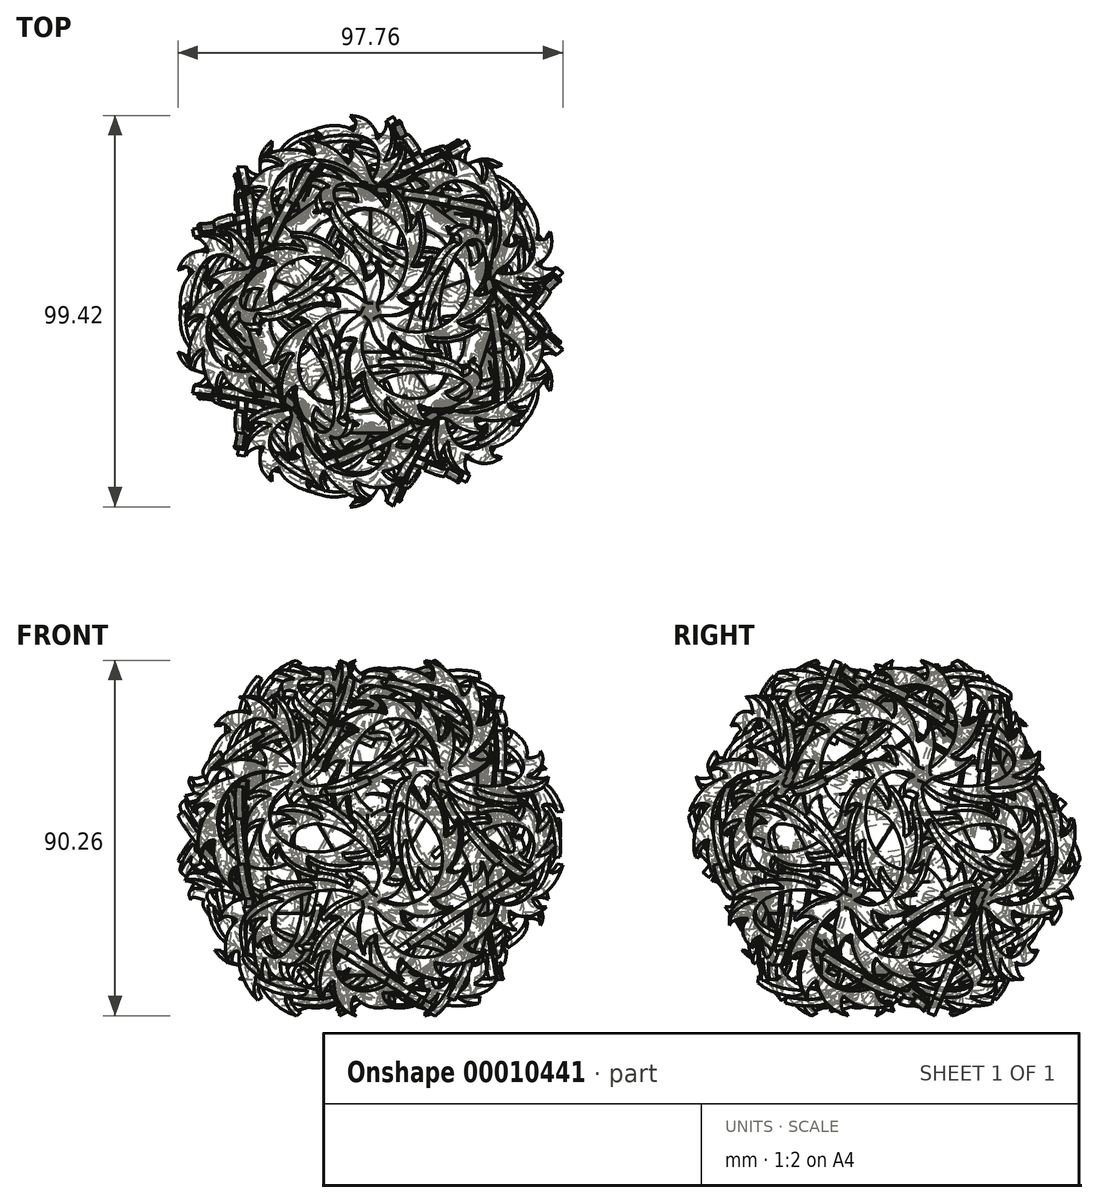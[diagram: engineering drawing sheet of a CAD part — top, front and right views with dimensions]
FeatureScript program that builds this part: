
annotation { "Feature Type Name" : "Feature", "Feature Type Description" : "" }
export const myFeature = defineFeature(function(context is Context, id is Id, definition is map)
    precondition{}
    {
        {
            var Q0;
            Q0=qCreatedBy(makeId("Top.planeOp"),FACE);
            var sketch = newSketch(context, id + "F0", { "sketchPlane" : qUnion([Q0])});
            skCircle(sketch, "E0.cCircle", {"center": v(0, 0) * mm, "radius": 10.32 * mm, "construction": true});
            skLineSegment(sketch, "E0.0", {"start": v(7.5, -10.32) * mm, "end": v(-7.5, -10.32) * mm});
            skLineSegment(sketch, "E0.1", {"start": v(-7.5, -10.32) * mm, "end": v(-12.14, 3.94) * mm});
            skLineSegment(sketch, "E0.2", {"start": v(-12.14, 3.94) * mm, "end": v(0, 12.76) * mm});
            skLineSegment(sketch, "E0.3", {"start": v(0, 12.76) * mm, "end": v(12.14, 3.94) * mm});
            skLineSegment(sketch, "E0.4", {"start": v(12.14, 3.94) * mm, "end": v(7.5, -10.32) * mm});
            skPoint(sketch, "E0.0.midPoint", {"position": v(0, -10.32) * mm});
            skLineSegment(sketch, "E1", {"start": v(0, 12.76) * mm, "end": v(0, -10.32) * mm});
            skSolve(sketch);
        }
        {
            var Q0;
            Q0=qCreatedBy(makeId("Top.planeOp"),FACE);
            var sketch = newSketch(context, id + "F1", { "sketchPlane" : qUnion([Q0])});
            skCircle(sketch, "E2.cCircle", {"center": v(22.17, -7.2) * mm, "radius": 13 * mm, "construction": true});
            skLineSegment(sketch, "E2.0", {"start": v(36.84, -4.09) * mm, "end": v(32.2, -18.35) * mm});
            skLineSegment(sketch, "E2.1", {"start": v(32.2, -18.35) * mm, "end": v(17.54, -21.47) * mm});
            skLineSegment(sketch, "E2.2", {"start": v(17.54, -21.47) * mm, "end": v(7.5, -10.32) * mm});
            skLineSegment(sketch, "E2.3", {"start": v(7.5, -10.32) * mm, "end": v(12.14, 3.94) * mm});
            skLineSegment(sketch, "E2.4", {"start": v(12.14, 3.94) * mm, "end": v(26.8, 7.06) * mm});
            skLineSegment(sketch, "E2.5", {"start": v(26.8, 7.06) * mm, "end": v(36.84, -4.09) * mm});
            skPoint(sketch, "E2.0.midPoint", {"position": v(34.53, -11.22) * mm});
            skSolve(sketch);
        }
        {
            var Q0;
            Q0=makeQuery(id+"F0.imprint","IMPRINT",FACE,{"disambiguationData":[TD([[makeQuery(id+"F0.imprint","IMPRINT",EDGE,{"derivedFrom":sQuery(id+"F0.wireOp",EDGE,"E0.0")}),-1.0]])]});
            extrude(context, id + "F2", {"entities" : qUnion([Q0]), "oppositeDirection" : true, "depth" : 1 * mm});
        }
        {
            var Q0;
            Q0=makeQuery(id+"F1.imprint","IMPRINT",FACE,{"disambiguationData":[TD([[makeQuery(id+"F1.imprint","IMPRINT",EDGE,{"derivedFrom":sQuery(id+"F1.wireOp",EDGE,"E2.0")}),-1.0]])]});
            extrude(context, id + "F3", {"entities" : qUnion([Q0]), "oppositeDirection" : true, "depth" : 1 * mm});
        }
        {
            var Q0;
            Q0=makeQuery(id+"F3.opExtrude","SWEPT_BODY",BODY,{"disambiguationData":[OSD([sQuery(id+"F1.wireOp",EDGE,"E2.0"),sQuery(id+"F1.wireOp",EDGE,"E2.1"),sQuery(id+"F1.wireOp",EDGE,"E2.2"),sQuery(id+"F1.wireOp",EDGE,"E2.3"),sQuery(id+"F1.wireOp",EDGE,"E2.4"),sQuery(id+"F1.wireOp",EDGE,"E2.5")])]});
            var Q1;
            Q1=makeQuery(id+"F2.opExtrude","CAP_EDGE",EDGE,{"disambiguationData":[OSD([sQuery(id+"F0.wireOp",EDGE,"E0.4")])],"isStart":true});
            transform(context, id + "F4", {"entities" : qUnion([Q0]), "transformType" : TransformType.ROTATION, "transformAxis" : qUnion([Q1]), "angle" : 37.38 * degree, "oppositeDirection" : true, "makeCopy" : false});
        }
        {
            var Q0;
            Q0=qCreatedBy(makeId("Right.planeOp"),FACE);
            var sketch = newSketch(context, id + "F5", { "sketchPlane" : qUnion([Q0])});
            skLineSegment(sketch, "E3", {"start": v(0, 0) * mm, "end": v(0, 7.73) * mm});
            skSolve(sketch);
        }
        {
            var Q0;
            Q0=makeQuery(id+"F3.opExtrude","SWEPT_BODY",BODY,{"disambiguationData":[OSD([sQuery(id+"F1.wireOp",EDGE,"E2.0"),sQuery(id+"F1.wireOp",EDGE,"E2.1"),sQuery(id+"F1.wireOp",EDGE,"E2.2"),sQuery(id+"F1.wireOp",EDGE,"E2.3"),sQuery(id+"F1.wireOp",EDGE,"E2.4"),sQuery(id+"F1.wireOp",EDGE,"E2.5")])]});
            var Q1;
            Q1=sQuery(id+"F5.wireOp",EDGE,"E3");
            circularPattern(context, id + "F6", {"entities" : qUnion([Q0]), "axis" : qUnion([Q1]), "angle" : 72 * degree, "instanceCount" : round(5)});
        }
        {
            var Q0;
            Q0=makeQuery(id+"F6.opPattern","COPY",FACE,{"derivedFrom":makeQuery(id+"F3.opExtrude","CAP_FACE",FACE,{"disambiguationData":[OSD([sQuery(id+"F1.wireOp",EDGE,"E2.0"),sQuery(id+"F1.wireOp",EDGE,"E2.1"),sQuery(id+"F1.wireOp",EDGE,"E2.2"),sQuery(id+"F1.wireOp",EDGE,"E2.3"),sQuery(id+"F1.wireOp",EDGE,"E2.4"),sQuery(id+"F1.wireOp",EDGE,"E2.5")])],"isStart":true}),"instanceName":"4"});
            var sketch = newSketch(context, id + "F7", { "sketchPlane" : qUnion([Q0])});
            skLineSegment(sketch, "E4", {"start": v(0, -34.18) * mm, "end": v(0, -8.2) * mm});
            skLineSegment(sketch, "E5", {"start": v(-15, -21.2) * mm, "end": v(15, -21.2) * mm});
            skCircle(sketch, "E6", {"center": v(0, -21.2) * mm, "radius": 3.24 * mm});
            skSolve(sketch);
        }
        {
            var Q0;
            Q0=qCreatedBy(makeId("Right.planeOp"),FACE);
            var sketch = newSketch(context, id + "F8", { "sketchPlane" : qUnion([Q0])});
            skArc(sketch, "E7.0", {"start": v(-1.37, 0) * mm, "mid": v(-18.04, 14.75) * mm, "end": v(-20.04, -7.42) * mm});
            skLineSegment(sketch, "E8", {"start": v(-20.04, -7.42) * mm, "end": v(-24.47, -10.8) * mm});
            skLineSegment(sketch, "E9", {"start": v(-1.37, 0) * mm, "end": v(0, 0) * mm});
            skArc(sketch, "E10", {"start": v(1.07, 1.27) * mm, "mid": v(3.46, 7.37) * mm, "end": v(2.5, 13.85) * mm});
            skArc(sketch, "E11", {"start": v(-0.8, 8.97) * mm, "mid": v(1.84, 10.74) * mm, "end": v(2.5, 13.85) * mm});
            skArc(sketch, "E12.1.0", {"start": v(-0.8, 8.97) * mm, "mid": v(-2.13, 15.94) * mm, "end": v(-6.98, 21.1) * mm});
            skArc(sketch, "E12.1.1", {"start": v(-6.75, 15.32) * mm, "mid": v(-5.72, 18.26) * mm, "end": v(-6.98, 21.1) * mm});
            skArc(sketch, "E12.2.0", {"start": v(-6.75, 15.32) * mm, "mid": v(-11.92, 20.18) * mm, "end": v(-18.89, 21.5) * mm});
            skArc(sketch, "E12.2.1", {"start": v(-15.3, 16.96) * mm, "mid": v(-16.2, 19.94) * mm, "end": v(-18.89, 21.5) * mm});
            skArc(sketch, "E12.3.0", {"start": v(-15.3, 16.96) * mm, "mid": v(-22.34, 17.85) * mm, "end": v(-28.75, 14.83) * mm});
            skArc(sketch, "E12.3.1", {"start": v(-23.18, 13.26) * mm, "mid": v(-25.66, 15.15) * mm, "end": v(-28.75, 14.83) * mm});
            skArc(sketch, "E12.4.0", {"start": v(-23.18, 13.26) * mm, "mid": v(-29.4, 9.84) * mm, "end": v(-32.81, 3.63) * mm});
            skArc(sketch, "E12.4.1", {"start": v(-27.38, 5.64) * mm, "mid": v(-30.5, 5.7) * mm, "end": v(-32.81, 3.63) * mm});
            skArc(sketch, "E12.5.0", {"start": v(-27.38, 5.64) * mm, "mid": v(-30.4, -0.78) * mm, "end": v(-29.51, -7.81) * mm});
            skArc(sketch, "E12.5.1", {"start": v(-26.3, -3) * mm, "mid": v(-28.86, -4.77) * mm, "end": v(-29.51, -7.81) * mm});
            skArc(sketch, "E12.6.0", {"start": v(-26.3, -3) * mm, "mid": v(-26.03, -7.06) * mm, "end": v(-24.49, -10.82) * mm});
            skArc(sketch, "E13", {"start": v(-24.49, -10.82) * mm, "mid": v(-20.56, -11.35) * mm, "end": v(-20.04, -7.42) * mm});
            skArc(sketch, "E14", {"start": v(-1.37, 0) * mm, "mid": v(1.27, -2.11) * mm, "end": v(1.07, 1.27) * mm});
            skSolve(sketch);
        }
        {
            var Q0;
            {var subQ2=sQuery(id+"F8.wireOp",EDGE,"E7.0");Q0=makeQuery(id+"F8.imprint","IMPRINT",FACE,{"disambiguationData":[TD([[makeQuery(id+"F8.imprint","IMPRINT",EDGE,{"derivedFrom":subQ2}),-1.0]])]});}
            extrude(context, id + "F9", {"entities" : qUnion([Q0]), "oppositeDirection" : true, "depth" : 2 * mm});
        }
        {
            var Q0;
            Q0=makeQuery(id+"F9.opExtrude","SWEPT_EDGE",EDGE,{"disambiguationData":[OSD([sQuery(id+"F8.wireOp",EDGE,"E10"),sQuery(id+"F8.wireOp",EDGE,"E14")])]});
            fillet(context, id + "F10", {"entities" : qUnion([Q0]), "radius" : 5 * mm, "tangentPropagation" : true, "allowEdgeOverflow" : false});
        }
        {
            var Q0;
            Q0=qCreatedBy(makeId("Right.planeOp"),FACE);
            var sketch = newSketch(context, id + "F11", { "sketchPlane" : qUnion([Q0])});
            skLineSegment(sketch, "E15", {"start": v(0, 0) * mm, "end": v(-20.65, -7.89) * mm});
            skLineSegment(sketch, "E16", {"start": v(0, 0) * mm, "end": v(0, 28.42) * mm});
            skSolve(sketch);
        }
        {
            var Q0;
            Q0=makeQuery(id+"F9.opExtrude","SWEPT_BODY",BODY,{"disambiguationData":[OSD([sQuery(id+"F8.wireOp",EDGE,"003f2e54-bd62-4f0b-a98e-8c36e71e2cf6"),sQuery(id+"F8.wireOp",EDGE,"8c729305-40a1-49fa-b790-4b99a3909bb6"),sQuery(id+"F8.wireOp",EDGE,"862a2a8f-3db7-4421-9c69-6ab2f53c4c24.1.0"),sQuery(id+"F8.wireOp",EDGE,"862a2a8f-3db7-4421-9c69-6ab2f53c4c24.1.1"),sQuery(id+"F8.wireOp",EDGE,"862a2a8f-3db7-4421-9c69-6ab2f53c4c24.2.0"),sQuery(id+"F8.wireOp",EDGE,"862a2a8f-3db7-4421-9c69-6ab2f53c4c24.2.1"),sQuery(id+"F8.wireOp",EDGE,"862a2a8f-3db7-4421-9c69-6ab2f53c4c24.3.0"),sQuery(id+"F8.wireOp",EDGE,"862a2a8f-3db7-4421-9c69-6ab2f53c4c24.3.1"),sQuery(id+"F8.wireOp",EDGE,"862a2a8f-3db7-4421-9c69-6ab2f53c4c24.4.0"),sQuery(id+"F8.wireOp",EDGE,"862a2a8f-3db7-4421-9c69-6ab2f53c4c24.4.1"),sQuery(id+"F8.wireOp",EDGE,"862a2a8f-3db7-4421-9c69-6ab2f53c4c24.5.0"),sQuery(id+"F8.wireOp",EDGE,"E7.0"),sQuery(id+"F8.wireOp",EDGE,"E8"),sQuery(id+"F8.wireOp",EDGE,"E9")])]});
            var Q1;
            Q1=sQuery(id+"F11.wireOp",EDGE,"E15");
            transform(context, id + "F12", {"entities" : qUnion([Q0]), "transformType" : TransformType.ROTATION, "transformAxis" : qUnion([Q1]), "angle" : 65 * degree, "makeCopy" : false});
        }
        {
            var Q0;
            Q0=makeQuery(id+"F9.opExtrude","SWEPT_BODY",BODY,{"disambiguationData":[OSD([sQuery(id+"F8.wireOp",EDGE,"003f2e54-bd62-4f0b-a98e-8c36e71e2cf6"),sQuery(id+"F8.wireOp",EDGE,"8c729305-40a1-49fa-b790-4b99a3909bb6"),sQuery(id+"F8.wireOp",EDGE,"862a2a8f-3db7-4421-9c69-6ab2f53c4c24.1.0"),sQuery(id+"F8.wireOp",EDGE,"862a2a8f-3db7-4421-9c69-6ab2f53c4c24.1.1"),sQuery(id+"F8.wireOp",EDGE,"862a2a8f-3db7-4421-9c69-6ab2f53c4c24.2.0"),sQuery(id+"F8.wireOp",EDGE,"862a2a8f-3db7-4421-9c69-6ab2f53c4c24.2.1"),sQuery(id+"F8.wireOp",EDGE,"862a2a8f-3db7-4421-9c69-6ab2f53c4c24.3.0"),sQuery(id+"F8.wireOp",EDGE,"862a2a8f-3db7-4421-9c69-6ab2f53c4c24.3.1"),sQuery(id+"F8.wireOp",EDGE,"862a2a8f-3db7-4421-9c69-6ab2f53c4c24.4.0"),sQuery(id+"F8.wireOp",EDGE,"862a2a8f-3db7-4421-9c69-6ab2f53c4c24.4.1"),sQuery(id+"F8.wireOp",EDGE,"862a2a8f-3db7-4421-9c69-6ab2f53c4c24.5.0"),sQuery(id+"F8.wireOp",EDGE,"E7.0"),sQuery(id+"F8.wireOp",EDGE,"E8"),sQuery(id+"F8.wireOp",EDGE,"E9")])]});
            var Q1;
            Q1=sQuery(id+"F11.wireOp",EDGE,"E16");
            circularPattern(context, id + "F13", {"entities" : qUnion([Q0]), "axis" : qUnion([Q1]), "angle" : 72 * degree, "instanceCount" : round(5)});
        }
        {
            var Q0;
            Q0=qCreatedBy(makeId("Right.planeOp"),FACE);
            var sketch = newSketch(context, id + "F14", { "sketchPlane" : qUnion([Q0])});
            skLineSegment(sketch, "E17.0", {"start": v(-30.97, -15.77) * mm, "end": v(-10.32, 0) * mm});
            skLineSegment(sketch, "E18", {"start": v(-20.65, -7.89) * mm, "end": v(-30.05, 4.42) * mm});
            skSolve(sketch);
        }
        {
            var Q0;
            Q0=makeQuery(id+"F9.opExtrude","SWEPT_BODY",BODY,{"disambiguationData":[OSD([sQuery(id+"F8.wireOp",EDGE,"003f2e54-bd62-4f0b-a98e-8c36e71e2cf6"),sQuery(id+"F8.wireOp",EDGE,"8c729305-40a1-49fa-b790-4b99a3909bb6"),sQuery(id+"F8.wireOp",EDGE,"862a2a8f-3db7-4421-9c69-6ab2f53c4c24.1.0"),sQuery(id+"F8.wireOp",EDGE,"862a2a8f-3db7-4421-9c69-6ab2f53c4c24.1.1"),sQuery(id+"F8.wireOp",EDGE,"862a2a8f-3db7-4421-9c69-6ab2f53c4c24.2.0"),sQuery(id+"F8.wireOp",EDGE,"862a2a8f-3db7-4421-9c69-6ab2f53c4c24.2.1"),sQuery(id+"F8.wireOp",EDGE,"862a2a8f-3db7-4421-9c69-6ab2f53c4c24.3.0"),sQuery(id+"F8.wireOp",EDGE,"862a2a8f-3db7-4421-9c69-6ab2f53c4c24.3.1"),sQuery(id+"F8.wireOp",EDGE,"862a2a8f-3db7-4421-9c69-6ab2f53c4c24.4.0"),sQuery(id+"F8.wireOp",EDGE,"862a2a8f-3db7-4421-9c69-6ab2f53c4c24.4.1"),sQuery(id+"F8.wireOp",EDGE,"862a2a8f-3db7-4421-9c69-6ab2f53c4c24.5.0"),sQuery(id+"F8.wireOp",EDGE,"E7.0"),sQuery(id+"F8.wireOp",EDGE,"E8"),sQuery(id+"F8.wireOp",EDGE,"E9")])]});
            var Q1;
            Q1=sQuery(id+"F14.wireOp",EDGE,"E18");
            circularPattern(context, id + "F15", {"entities" : qUnion([Q0]), "axis" : qUnion([Q1]), "angle" : 120 * degree, "instanceCount" : round(3)});
        }
        {
            var Q0;
            Q0=makeQuery(id+"F15.opPattern","COPY",BODY,{"derivedFrom":makeQuery(id+"F9.opExtrude","SWEPT_BODY",BODY,{"disambiguationData":[OSD([sQuery(id+"F8.wireOp",EDGE,"E7.0"),sQuery(id+"F8.wireOp",EDGE,"E10"),sQuery(id+"F8.wireOp",EDGE,"E11"),sQuery(id+"F8.wireOp",EDGE,"E12.1.0"),sQuery(id+"F8.wireOp",EDGE,"E12.1.1"),sQuery(id+"F8.wireOp",EDGE,"E12.2.0"),sQuery(id+"F8.wireOp",EDGE,"E12.2.1"),sQuery(id+"F8.wireOp",EDGE,"E12.3.0"),sQuery(id+"F8.wireOp",EDGE,"E12.3.1"),sQuery(id+"F8.wireOp",EDGE,"E12.4.0"),sQuery(id+"F8.wireOp",EDGE,"E12.4.1"),sQuery(id+"F8.wireOp",EDGE,"E12.5.0"),sQuery(id+"F8.wireOp",EDGE,"E12.5.1"),sQuery(id+"F8.wireOp",EDGE,"E12.6.0"),sQuery(id+"F8.wireOp",EDGE,"E13"),sQuery(id+"F8.wireOp",EDGE,"E14")])]}),"instanceName":"2"});
            var Q1;
            Q1=makeQuery(id+"F15.opPattern","COPY",BODY,{"derivedFrom":makeQuery(id+"F9.opExtrude","SWEPT_BODY",BODY,{"disambiguationData":[OSD([sQuery(id+"F8.wireOp",EDGE,"E7.0"),sQuery(id+"F8.wireOp",EDGE,"E10"),sQuery(id+"F8.wireOp",EDGE,"E11"),sQuery(id+"F8.wireOp",EDGE,"E12.1.0"),sQuery(id+"F8.wireOp",EDGE,"E12.1.1"),sQuery(id+"F8.wireOp",EDGE,"E12.2.0"),sQuery(id+"F8.wireOp",EDGE,"E12.2.1"),sQuery(id+"F8.wireOp",EDGE,"E12.3.0"),sQuery(id+"F8.wireOp",EDGE,"E12.3.1"),sQuery(id+"F8.wireOp",EDGE,"E12.4.0"),sQuery(id+"F8.wireOp",EDGE,"E12.4.1"),sQuery(id+"F8.wireOp",EDGE,"E12.5.0"),sQuery(id+"F8.wireOp",EDGE,"E12.5.1"),sQuery(id+"F8.wireOp",EDGE,"E12.6.0"),sQuery(id+"F8.wireOp",EDGE,"E13"),sQuery(id+"F8.wireOp",EDGE,"E14")])]}),"instanceName":"1"});
            var Q2;
            Q2=sQuery(id+"F11.wireOp",EDGE,"E16");
            circularPattern(context, id + "F16", {"entities" : qUnion([Q0, Q1]), "axis" : qUnion([Q2]), "angle" : 72 * degree, "instanceCount" : round(5)});
        }
        {
            var Q0;
            Q0=makeQuery(id+"F3.opExtrude","SWEPT_BODY",BODY,{"disambiguationData":[OSD([sQuery(id+"F1.wireOp",EDGE,"E2.0"),sQuery(id+"F1.wireOp",EDGE,"E2.1"),sQuery(id+"F1.wireOp",EDGE,"E2.2"),sQuery(id+"F1.wireOp",EDGE,"E2.3"),sQuery(id+"F1.wireOp",EDGE,"E2.4"),sQuery(id+"F1.wireOp",EDGE,"E2.5")])]});
            var Q1;
            Q1=makeQuery(id+"F16.opPattern","COPY",BODY,{"derivedFrom":makeQuery(id+"F15.opPattern","COPY",BODY,{"derivedFrom":makeQuery(id+"F9.opExtrude","SWEPT_BODY",BODY,{"disambiguationData":[OSD([sQuery(id+"F8.wireOp",EDGE,"E7.0"),sQuery(id+"F8.wireOp",EDGE,"E10"),sQuery(id+"F8.wireOp",EDGE,"E11"),sQuery(id+"F8.wireOp",EDGE,"E12.1.0"),sQuery(id+"F8.wireOp",EDGE,"E12.1.1"),sQuery(id+"F8.wireOp",EDGE,"E12.2.0"),sQuery(id+"F8.wireOp",EDGE,"E12.2.1"),sQuery(id+"F8.wireOp",EDGE,"E12.3.0"),sQuery(id+"F8.wireOp",EDGE,"E12.3.1"),sQuery(id+"F8.wireOp",EDGE,"E12.4.0"),sQuery(id+"F8.wireOp",EDGE,"E12.4.1"),sQuery(id+"F8.wireOp",EDGE,"E12.5.0"),sQuery(id+"F8.wireOp",EDGE,"E12.5.1"),sQuery(id+"F8.wireOp",EDGE,"E12.6.0"),sQuery(id+"F8.wireOp",EDGE,"E13"),sQuery(id+"F8.wireOp",EDGE,"E14")])]}),"instanceName":"1"}),"instanceName":"1"});
            var Q2;
            Q2=makeQuery(id+"F13.opPattern","COPY",BODY,{"derivedFrom":makeQuery(id+"F9.opExtrude","SWEPT_BODY",BODY,{"disambiguationData":[OSD([sQuery(id+"F8.wireOp",EDGE,"E7.0"),sQuery(id+"F8.wireOp",EDGE,"E10"),sQuery(id+"F8.wireOp",EDGE,"E11"),sQuery(id+"F8.wireOp",EDGE,"E12.1.0"),sQuery(id+"F8.wireOp",EDGE,"E12.1.1"),sQuery(id+"F8.wireOp",EDGE,"E12.2.0"),sQuery(id+"F8.wireOp",EDGE,"E12.2.1"),sQuery(id+"F8.wireOp",EDGE,"E12.3.0"),sQuery(id+"F8.wireOp",EDGE,"E12.3.1"),sQuery(id+"F8.wireOp",EDGE,"E12.4.0"),sQuery(id+"F8.wireOp",EDGE,"E12.4.1"),sQuery(id+"F8.wireOp",EDGE,"E12.5.0"),sQuery(id+"F8.wireOp",EDGE,"E12.5.1"),sQuery(id+"F8.wireOp",EDGE,"E12.6.0"),sQuery(id+"F8.wireOp",EDGE,"E13"),sQuery(id+"F8.wireOp",EDGE,"E14")])]}),"instanceName":"1"});
            var Q3;
            Q3=makeQuery(id+"F16.opPattern","COPY",BODY,{"derivedFrom":makeQuery(id+"F15.opPattern","COPY",BODY,{"derivedFrom":makeQuery(id+"F9.opExtrude","SWEPT_BODY",BODY,{"disambiguationData":[OSD([sQuery(id+"F8.wireOp",EDGE,"E7.0"),sQuery(id+"F8.wireOp",EDGE,"E10"),sQuery(id+"F8.wireOp",EDGE,"E11"),sQuery(id+"F8.wireOp",EDGE,"E12.1.0"),sQuery(id+"F8.wireOp",EDGE,"E12.1.1"),sQuery(id+"F8.wireOp",EDGE,"E12.2.0"),sQuery(id+"F8.wireOp",EDGE,"E12.2.1"),sQuery(id+"F8.wireOp",EDGE,"E12.3.0"),sQuery(id+"F8.wireOp",EDGE,"E12.3.1"),sQuery(id+"F8.wireOp",EDGE,"E12.4.0"),sQuery(id+"F8.wireOp",EDGE,"E12.4.1"),sQuery(id+"F8.wireOp",EDGE,"E12.5.0"),sQuery(id+"F8.wireOp",EDGE,"E12.5.1"),sQuery(id+"F8.wireOp",EDGE,"E12.6.0"),sQuery(id+"F8.wireOp",EDGE,"E13"),sQuery(id+"F8.wireOp",EDGE,"E14")])]}),"instanceName":"2"}),"instanceName":"1"});
            var Q4;
            Q4=sQuery(id+"F14.wireOp",EDGE,"E18");
            circularPattern(context, id + "F17", {"entities" : qUnion([Q0, Q1, Q2, Q3]), "axis" : qUnion([Q4]), "angle" : 120 * degree, "instanceCount" : 2, "oppositeDirection" : true});
        }
        {
            var Q0;
            Q0=makeQuery(id+"F2.opExtrude","SWEPT_BODY",BODY,{"disambiguationData":[OSD([sQuery(id+"F0.wireOp",EDGE,"E0.0"),sQuery(id+"F0.wireOp",EDGE,"E0.1"),sQuery(id+"F0.wireOp",EDGE,"E0.2"),sQuery(id+"F0.wireOp",EDGE,"E0.3"),sQuery(id+"F0.wireOp",EDGE,"E0.4")])]});
            var Q1;
            Q1=makeQuery(id+"F13.opPattern","COPY",BODY,{"derivedFrom":makeQuery(id+"F9.opExtrude","SWEPT_BODY",BODY,{"disambiguationData":[OSD([sQuery(id+"F8.wireOp",EDGE,"E7.0"),sQuery(id+"F8.wireOp",EDGE,"E10"),sQuery(id+"F8.wireOp",EDGE,"E11"),sQuery(id+"F8.wireOp",EDGE,"E12.1.0"),sQuery(id+"F8.wireOp",EDGE,"E12.1.1"),sQuery(id+"F8.wireOp",EDGE,"E12.2.0"),sQuery(id+"F8.wireOp",EDGE,"E12.2.1"),sQuery(id+"F8.wireOp",EDGE,"E12.3.0"),sQuery(id+"F8.wireOp",EDGE,"E12.3.1"),sQuery(id+"F8.wireOp",EDGE,"E12.4.0"),sQuery(id+"F8.wireOp",EDGE,"E12.4.1"),sQuery(id+"F8.wireOp",EDGE,"E12.5.0"),sQuery(id+"F8.wireOp",EDGE,"E12.5.1"),sQuery(id+"F8.wireOp",EDGE,"E12.6.0"),sQuery(id+"F8.wireOp",EDGE,"E13"),sQuery(id+"F8.wireOp",EDGE,"E14")])]}),"instanceName":"2"});
            var Q2;
            Q2=makeQuery(id+"F13.opPattern","COPY",BODY,{"derivedFrom":makeQuery(id+"F9.opExtrude","SWEPT_BODY",BODY,{"disambiguationData":[OSD([sQuery(id+"F8.wireOp",EDGE,"E7.0"),sQuery(id+"F8.wireOp",EDGE,"E10"),sQuery(id+"F8.wireOp",EDGE,"E11"),sQuery(id+"F8.wireOp",EDGE,"E12.1.0"),sQuery(id+"F8.wireOp",EDGE,"E12.1.1"),sQuery(id+"F8.wireOp",EDGE,"E12.2.0"),sQuery(id+"F8.wireOp",EDGE,"E12.2.1"),sQuery(id+"F8.wireOp",EDGE,"E12.3.0"),sQuery(id+"F8.wireOp",EDGE,"E12.3.1"),sQuery(id+"F8.wireOp",EDGE,"E12.4.0"),sQuery(id+"F8.wireOp",EDGE,"E12.4.1"),sQuery(id+"F8.wireOp",EDGE,"E12.5.0"),sQuery(id+"F8.wireOp",EDGE,"E12.5.1"),sQuery(id+"F8.wireOp",EDGE,"E12.6.0"),sQuery(id+"F8.wireOp",EDGE,"E13"),sQuery(id+"F8.wireOp",EDGE,"E14")])]}),"instanceName":"3"});
            var Q3;
            Q3=sQuery(id+"F14.wireOp",EDGE,"E18");
            circularPattern(context, id + "F18", {"entities" : qUnion([Q0, Q1, Q2]), "axis" : qUnion([Q3]), "angle" : 120 * degree, "instanceCount" : round(3)});
        }
        {
            var Q0;
            Q0=makeQuery(id+"F18.opPattern","COPY",FACE,{"derivedFrom":makeQuery(id+"F2.opExtrude","CAP_FACE",FACE,{"disambiguationData":[OSD([sQuery(id+"F0.wireOp",EDGE,"E0.0"),sQuery(id+"F0.wireOp",EDGE,"E0.1"),sQuery(id+"F0.wireOp",EDGE,"E0.2"),sQuery(id+"F0.wireOp",EDGE,"E0.3"),sQuery(id+"F0.wireOp",EDGE,"E0.4")])],"isStart":true}),"instanceName":"1"});
            var sketch = newSketch(context, id + "F19", { "sketchPlane" : qUnion([Q0])});
            skLineSegment(sketch, "E19", {"start": v(-1.3, -23.63) * mm, "end": v(-19.97, -37.2) * mm});
            skLineSegment(sketch, "E20", {"start": v(-19.97, -22.2) * mm, "end": v(-1.3, -35.77) * mm});
            skSolve(sketch);
        }
        {
            var Q0;
            Q0=sQuery(id+"F19.wireOp",VERTEX,"E19.end");
            var Q1;
            Q1=sQuery(id+"F19.wireOp",VERTEX,"E19.start");
            var Q2;
            Q2=sQuery(id+"F14.wireOp",VERTEX,"E18.end");
            cPlane(context, id + "F20", {"entities" : qUnion([Q0, Q1, Q2]), "cplaneType" : CPlaneType.THREE_POINT, "offset" : 150 * mm, "width" : 150 * mm, "height" : 150 * mm});
        }
        {
            var Q0;
            Q0=qCreatedBy(id+"F20.planeOp",FACE);
            var sketch = newSketch(context, id + "F21", { "sketchPlane" : qUnion([Q0])});
            skLineSegment(sketch, "E21.0", {"start": v(23.59, 6.27) * mm, "end": v(41.93, -7.75) * mm});
            skLineSegment(sketch, "E21.1", {"start": v(34.92, -2.4) * mm, "end": v(29.26, 1.94) * mm});
            skLineSegment(sketch, "E22", {"start": v(31.8, 0) * mm, "end": v(33.22, 1.87) * mm});
            skLineSegment(sketch, "E23", {"start": v(33.22, 1.87) * mm, "end": v(37.58, 7.58) * mm});
            skSolve(sketch);
        }
        {
            var Q0;
            Q0=makeQuery(id+"F17.opPattern","COPY",BODY,{"derivedFrom":makeQuery(id+"F3.opExtrude","SWEPT_BODY",BODY,{"disambiguationData":[OSD([sQuery(id+"F1.wireOp",EDGE,"E2.0"),sQuery(id+"F1.wireOp",EDGE,"E2.1"),sQuery(id+"F1.wireOp",EDGE,"E2.2"),sQuery(id+"F1.wireOp",EDGE,"E2.3"),sQuery(id+"F1.wireOp",EDGE,"E2.4"),sQuery(id+"F1.wireOp",EDGE,"E2.5")])]}),"instanceName":"1"});
            var Q1;
            Q1=makeQuery(id+"F17.opPattern","COPY",BODY,{"derivedFrom":makeQuery(id+"F13.opPattern","COPY",BODY,{"derivedFrom":makeQuery(id+"F9.opExtrude","SWEPT_BODY",BODY,{"disambiguationData":[OSD([sQuery(id+"F8.wireOp",EDGE,"E7.0"),sQuery(id+"F8.wireOp",EDGE,"E10"),sQuery(id+"F8.wireOp",EDGE,"E11"),sQuery(id+"F8.wireOp",EDGE,"E12.1.0"),sQuery(id+"F8.wireOp",EDGE,"E12.1.1"),sQuery(id+"F8.wireOp",EDGE,"E12.2.0"),sQuery(id+"F8.wireOp",EDGE,"E12.2.1"),sQuery(id+"F8.wireOp",EDGE,"E12.3.0"),sQuery(id+"F8.wireOp",EDGE,"E12.3.1"),sQuery(id+"F8.wireOp",EDGE,"E12.4.0"),sQuery(id+"F8.wireOp",EDGE,"E12.4.1"),sQuery(id+"F8.wireOp",EDGE,"E12.5.0"),sQuery(id+"F8.wireOp",EDGE,"E12.5.1"),sQuery(id+"F8.wireOp",EDGE,"E12.6.0"),sQuery(id+"F8.wireOp",EDGE,"E13"),sQuery(id+"F8.wireOp",EDGE,"E14")])]}),"instanceName":"1"}),"instanceName":"1"});
            var Q2;
            Q2=makeQuery(id+"F17.opPattern","COPY",BODY,{"derivedFrom":makeQuery(id+"F16.opPattern","COPY",BODY,{"derivedFrom":makeQuery(id+"F15.opPattern","COPY",BODY,{"derivedFrom":makeQuery(id+"F9.opExtrude","SWEPT_BODY",BODY,{"disambiguationData":[OSD([sQuery(id+"F8.wireOp",EDGE,"E7.0"),sQuery(id+"F8.wireOp",EDGE,"E10"),sQuery(id+"F8.wireOp",EDGE,"E11"),sQuery(id+"F8.wireOp",EDGE,"E12.1.0"),sQuery(id+"F8.wireOp",EDGE,"E12.1.1"),sQuery(id+"F8.wireOp",EDGE,"E12.2.0"),sQuery(id+"F8.wireOp",EDGE,"E12.2.1"),sQuery(id+"F8.wireOp",EDGE,"E12.3.0"),sQuery(id+"F8.wireOp",EDGE,"E12.3.1"),sQuery(id+"F8.wireOp",EDGE,"E12.4.0"),sQuery(id+"F8.wireOp",EDGE,"E12.4.1"),sQuery(id+"F8.wireOp",EDGE,"E12.5.0"),sQuery(id+"F8.wireOp",EDGE,"E12.5.1"),sQuery(id+"F8.wireOp",EDGE,"E12.6.0"),sQuery(id+"F8.wireOp",EDGE,"E13"),sQuery(id+"F8.wireOp",EDGE,"E14")])]}),"instanceName":"2"}),"instanceName":"1"}),"instanceName":"1"});
            var Q3;
            Q3=makeQuery(id+"F17.opPattern","COPY",BODY,{"derivedFrom":makeQuery(id+"F16.opPattern","COPY",BODY,{"derivedFrom":makeQuery(id+"F15.opPattern","COPY",BODY,{"derivedFrom":makeQuery(id+"F9.opExtrude","SWEPT_BODY",BODY,{"disambiguationData":[OSD([sQuery(id+"F8.wireOp",EDGE,"E7.0"),sQuery(id+"F8.wireOp",EDGE,"E10"),sQuery(id+"F8.wireOp",EDGE,"E11"),sQuery(id+"F8.wireOp",EDGE,"E12.1.0"),sQuery(id+"F8.wireOp",EDGE,"E12.1.1"),sQuery(id+"F8.wireOp",EDGE,"E12.2.0"),sQuery(id+"F8.wireOp",EDGE,"E12.2.1"),sQuery(id+"F8.wireOp",EDGE,"E12.3.0"),sQuery(id+"F8.wireOp",EDGE,"E12.3.1"),sQuery(id+"F8.wireOp",EDGE,"E12.4.0"),sQuery(id+"F8.wireOp",EDGE,"E12.4.1"),sQuery(id+"F8.wireOp",EDGE,"E12.5.0"),sQuery(id+"F8.wireOp",EDGE,"E12.5.1"),sQuery(id+"F8.wireOp",EDGE,"E12.6.0"),sQuery(id+"F8.wireOp",EDGE,"E13"),sQuery(id+"F8.wireOp",EDGE,"E14")])]}),"instanceName":"1"}),"instanceName":"1"}),"instanceName":"1"});
            var Q4;
            Q4=sQuery(id+"F21.wireOp",EDGE,"E22");
            circularPattern(context, id + "F22", {"entities" : qUnion([Q0, Q1, Q2, Q3]), "axis" : qUnion([Q4]), "angle" : 72 * degree, "instanceCount" : round(3), "oppositeDirection" : true});
        }
        {
            var Q0;
            Q0=makeQuery(id+"F18.opPattern","COPY",FACE,{"derivedFrom":makeQuery(id+"F2.opExtrude","CAP_FACE",FACE,{"disambiguationData":[OSD([sQuery(id+"F0.wireOp",EDGE,"E0.0"),sQuery(id+"F0.wireOp",EDGE,"E0.1"),sQuery(id+"F0.wireOp",EDGE,"E0.2"),sQuery(id+"F0.wireOp",EDGE,"E0.3"),sQuery(id+"F0.wireOp",EDGE,"E0.4")])],"isStart":true}),"instanceName":"2"});
            var sketch = newSketch(context, id + "F23", { "sketchPlane" : qUnion([Q0])});
            skLineSegment(sketch, "E24", {"start": v(1.3, -23.63) * mm, "end": v(19.97, -37.2) * mm});
            skLineSegment(sketch, "E25", {"start": v(5.7, -41.83) * mm, "end": v(12.84, -19.88) * mm});
            skSolve(sketch);
        }
        {
            var Q0;
            Q0=sQuery(id+"F23.wireOp",VERTEX,"E24.end");
            var Q1;
            Q1=sQuery(id+"F23.wireOp",VERTEX,"E24.start");
            var Q2;
            Q2=sQuery(id+"F14.wireOp",VERTEX,"E18.end");
            cPlane(context, id + "F24", {"entities" : qUnion([Q0, Q1, Q2]), "cplaneType" : CPlaneType.THREE_POINT, "offset" : 150 * mm, "width" : 150 * mm, "height" : 150 * mm});
        }
        {
            var Q0;
            Q0=qCreatedBy(id+"F24.planeOp",FACE);
            var sketch = newSketch(context, id + "F25", { "sketchPlane" : qUnion([Q0])});
            skLineSegment(sketch, "E26.0", {"start": v(23.59, 6.27) * mm, "end": v(41.93, -7.75) * mm});
            skLineSegment(sketch, "E26.1", {"start": v(34.92, -2.4) * mm, "end": v(29.26, 1.94) * mm});
            skLineSegment(sketch, "E27", {"start": v(31.8, 0) * mm, "end": v(36.23, 5.8) * mm});
            skSolve(sketch);
        }
        {
            var Q0;
            Q0=makeQuery(id+"F3.opExtrude","SWEPT_BODY",BODY,{"disambiguationData":[OSD([sQuery(id+"F1.wireOp",EDGE,"E2.0"),sQuery(id+"F1.wireOp",EDGE,"E2.1"),sQuery(id+"F1.wireOp",EDGE,"E2.2"),sQuery(id+"F1.wireOp",EDGE,"E2.3"),sQuery(id+"F1.wireOp",EDGE,"E2.4"),sQuery(id+"F1.wireOp",EDGE,"E2.5")])]});
            var Q1;
            Q1=makeQuery(id+"F16.opPattern","COPY",BODY,{"derivedFrom":makeQuery(id+"F15.opPattern","COPY",BODY,{"derivedFrom":makeQuery(id+"F9.opExtrude","SWEPT_BODY",BODY,{"disambiguationData":[OSD([sQuery(id+"F8.wireOp",EDGE,"E7.0"),sQuery(id+"F8.wireOp",EDGE,"E10"),sQuery(id+"F8.wireOp",EDGE,"E11"),sQuery(id+"F8.wireOp",EDGE,"E12.1.0"),sQuery(id+"F8.wireOp",EDGE,"E12.1.1"),sQuery(id+"F8.wireOp",EDGE,"E12.2.0"),sQuery(id+"F8.wireOp",EDGE,"E12.2.1"),sQuery(id+"F8.wireOp",EDGE,"E12.3.0"),sQuery(id+"F8.wireOp",EDGE,"E12.3.1"),sQuery(id+"F8.wireOp",EDGE,"E12.4.0"),sQuery(id+"F8.wireOp",EDGE,"E12.4.1"),sQuery(id+"F8.wireOp",EDGE,"E12.5.0"),sQuery(id+"F8.wireOp",EDGE,"E12.5.1"),sQuery(id+"F8.wireOp",EDGE,"E12.6.0"),sQuery(id+"F8.wireOp",EDGE,"E13"),sQuery(id+"F8.wireOp",EDGE,"E14")])]}),"instanceName":"2"}),"instanceName":"1"});
            var Q2;
            Q2=makeQuery(id+"F13.opPattern","COPY",BODY,{"derivedFrom":makeQuery(id+"F9.opExtrude","SWEPT_BODY",BODY,{"disambiguationData":[OSD([sQuery(id+"F8.wireOp",EDGE,"E7.0"),sQuery(id+"F8.wireOp",EDGE,"E10"),sQuery(id+"F8.wireOp",EDGE,"E11"),sQuery(id+"F8.wireOp",EDGE,"E12.1.0"),sQuery(id+"F8.wireOp",EDGE,"E12.1.1"),sQuery(id+"F8.wireOp",EDGE,"E12.2.0"),sQuery(id+"F8.wireOp",EDGE,"E12.2.1"),sQuery(id+"F8.wireOp",EDGE,"E12.3.0"),sQuery(id+"F8.wireOp",EDGE,"E12.3.1"),sQuery(id+"F8.wireOp",EDGE,"E12.4.0"),sQuery(id+"F8.wireOp",EDGE,"E12.4.1"),sQuery(id+"F8.wireOp",EDGE,"E12.5.0"),sQuery(id+"F8.wireOp",EDGE,"E12.5.1"),sQuery(id+"F8.wireOp",EDGE,"E12.6.0"),sQuery(id+"F8.wireOp",EDGE,"E13"),sQuery(id+"F8.wireOp",EDGE,"E14")])]}),"instanceName":"1"});
            var Q3;
            Q3=makeQuery(id+"F16.opPattern","COPY",BODY,{"derivedFrom":makeQuery(id+"F15.opPattern","COPY",BODY,{"derivedFrom":makeQuery(id+"F9.opExtrude","SWEPT_BODY",BODY,{"disambiguationData":[OSD([sQuery(id+"F8.wireOp",EDGE,"E7.0"),sQuery(id+"F8.wireOp",EDGE,"E10"),sQuery(id+"F8.wireOp",EDGE,"E11"),sQuery(id+"F8.wireOp",EDGE,"E12.1.0"),sQuery(id+"F8.wireOp",EDGE,"E12.1.1"),sQuery(id+"F8.wireOp",EDGE,"E12.2.0"),sQuery(id+"F8.wireOp",EDGE,"E12.2.1"),sQuery(id+"F8.wireOp",EDGE,"E12.3.0"),sQuery(id+"F8.wireOp",EDGE,"E12.3.1"),sQuery(id+"F8.wireOp",EDGE,"E12.4.0"),sQuery(id+"F8.wireOp",EDGE,"E12.4.1"),sQuery(id+"F8.wireOp",EDGE,"E12.5.0"),sQuery(id+"F8.wireOp",EDGE,"E12.5.1"),sQuery(id+"F8.wireOp",EDGE,"E12.6.0"),sQuery(id+"F8.wireOp",EDGE,"E13"),sQuery(id+"F8.wireOp",EDGE,"E14")])]}),"instanceName":"1"}),"instanceName":"1"});
            var Q4;
            Q4=sQuery(id+"F25.wireOp",EDGE,"E27");
            circularPattern(context, id + "F26", {"entities" : qUnion([Q0, Q1, Q2, Q3]), "axis" : qUnion([Q4]), "angle" : 72 * degree, "instanceCount" : round(3), "oppositeDirection" : true});
        }
        {
            var Q0;
            Q0=makeQuery(id+"F17.opPattern","COPY",FACE,{"derivedFrom":makeQuery(id+"F3.opExtrude","CAP_FACE",FACE,{"disambiguationData":[OSD([sQuery(id+"F1.wireOp",EDGE,"E2.0"),sQuery(id+"F1.wireOp",EDGE,"E2.1"),sQuery(id+"F1.wireOp",EDGE,"E2.2"),sQuery(id+"F1.wireOp",EDGE,"E2.3"),sQuery(id+"F1.wireOp",EDGE,"E2.4"),sQuery(id+"F1.wireOp",EDGE,"E2.5")])],"isStart":true}),"instanceName":"1"});
            var sketch = newSketch(context, id + "F27", { "sketchPlane" : qUnion([Q0])});
            skLineSegment(sketch, "E28", {"start": v(0, -47.28) * mm, "end": v(0, -21.3) * mm});
            skSolve(sketch);
        }
        {
            var Q0;
            Q0=qCreatedBy(makeId("Right.planeOp"),FACE);
            var sketch = newSketch(context, id + "F28", { "sketchPlane" : qUnion([Q0])});
            skLineSegment(sketch, "E29.0", {"start": v(-35.84, -41.3) * mm, "end": v(-30.97, -15.77) * mm});
            skLineSegment(sketch, "E30", {"start": v(-33.4, -28.53) * mm, "end": v(-47.6, -25.82) * mm});
            skSolve(sketch);
        }
        {
            var Q0;
            Q0=makeQuery(id+"F18.opPattern","COPY",BODY,{"derivedFrom":makeQuery(id+"F2.opExtrude","SWEPT_BODY",BODY,{"disambiguationData":[OSD([sQuery(id+"F0.wireOp",EDGE,"E0.0"),sQuery(id+"F0.wireOp",EDGE,"E0.1"),sQuery(id+"F0.wireOp",EDGE,"E0.2"),sQuery(id+"F0.wireOp",EDGE,"E0.3"),sQuery(id+"F0.wireOp",EDGE,"E0.4")])]}),"instanceName":"2"});
            var Q1;
            Q1=sQuery(id+"F28.wireOp",EDGE,"E30");
            circularPattern(context, id + "F29", {"entities" : qUnion([Q0]), "axis" : qUnion([Q1]), "angle" : 120 * degree, "instanceCount" : 2, "oppositeDirection" : true});
        }
        {
            var Q0;
            Q0=makeQuery(id+"F29.opPattern","COPY",FACE,{"derivedFrom":makeQuery(id+"F18.opPattern","COPY",FACE,{"derivedFrom":makeQuery(id+"F2.opExtrude","CAP_FACE",FACE,{"disambiguationData":[OSD([sQuery(id+"F0.wireOp",EDGE,"E0.0"),sQuery(id+"F0.wireOp",EDGE,"E0.1"),sQuery(id+"F0.wireOp",EDGE,"E0.2"),sQuery(id+"F0.wireOp",EDGE,"E0.3"),sQuery(id+"F0.wireOp",EDGE,"E0.4")])],"isStart":true}),"instanceName":"2"}),"instanceName":"1"});
            var sketch = newSketch(context, id + "F30", { "sketchPlane" : qUnion([Q0])});
            skLineSegment(sketch, "E31", {"start": v(0, -43.99) * mm, "end": v(0, -31.23) * mm});
            skLineSegment(sketch, "E32", {"start": v(-12.14, -35.17) * mm, "end": v(9.82, -28.04) * mm});
            skPoint(sketch, "E33.orphan", {"position": v(0, -20.9) * mm});
            skSolve(sketch);
        }
        {
            var Q0;
            Q0=qCreatedBy(makeId("Right.planeOp"),FACE);
            var sketch = newSketch(context, id + "F31", { "sketchPlane" : qUnion([Q0])});
            skLineSegment(sketch, "E34.0", {"start": v(-25.52, -61.94) * mm, "end": v(-31.23, -50.52) * mm});
            skLineSegment(sketch, "E35", {"start": v(-31.23, -50.52) * mm, "end": v(-51.07, -60.45) * mm});
            skSolve(sketch);
        }
        {
            var Q0;
            Q0=makeQuery(id+"F26.opPattern","COPY",BODY,{"derivedFrom":makeQuery(id+"F3.opExtrude","SWEPT_BODY",BODY,{"disambiguationData":[OSD([sQuery(id+"F1.wireOp",EDGE,"E2.0"),sQuery(id+"F1.wireOp",EDGE,"E2.1"),sQuery(id+"F1.wireOp",EDGE,"E2.2"),sQuery(id+"F1.wireOp",EDGE,"E2.3"),sQuery(id+"F1.wireOp",EDGE,"E2.4"),sQuery(id+"F1.wireOp",EDGE,"E2.5")])]}),"instanceName":"2"});
            var Q1;
            Q1=makeQuery(id+"F26.opPattern","COPY",BODY,{"derivedFrom":makeQuery(id+"F16.opPattern","COPY",BODY,{"derivedFrom":makeQuery(id+"F15.opPattern","COPY",BODY,{"derivedFrom":makeQuery(id+"F9.opExtrude","SWEPT_BODY",BODY,{"disambiguationData":[OSD([sQuery(id+"F8.wireOp",EDGE,"E7.0"),sQuery(id+"F8.wireOp",EDGE,"E10"),sQuery(id+"F8.wireOp",EDGE,"E11"),sQuery(id+"F8.wireOp",EDGE,"E12.1.0"),sQuery(id+"F8.wireOp",EDGE,"E12.1.1"),sQuery(id+"F8.wireOp",EDGE,"E12.2.0"),sQuery(id+"F8.wireOp",EDGE,"E12.2.1"),sQuery(id+"F8.wireOp",EDGE,"E12.3.0"),sQuery(id+"F8.wireOp",EDGE,"E12.3.1"),sQuery(id+"F8.wireOp",EDGE,"E12.4.0"),sQuery(id+"F8.wireOp",EDGE,"E12.4.1"),sQuery(id+"F8.wireOp",EDGE,"E12.5.0"),sQuery(id+"F8.wireOp",EDGE,"E12.5.1"),sQuery(id+"F8.wireOp",EDGE,"E12.6.0"),sQuery(id+"F8.wireOp",EDGE,"E13"),sQuery(id+"F8.wireOp",EDGE,"E14")])]}),"instanceName":"2"}),"instanceName":"1"}),"instanceName":"2"});
            var Q2;
            Q2=makeQuery(id+"F26.opPattern","COPY",BODY,{"derivedFrom":makeQuery(id+"F13.opPattern","COPY",BODY,{"derivedFrom":makeQuery(id+"F9.opExtrude","SWEPT_BODY",BODY,{"disambiguationData":[OSD([sQuery(id+"F8.wireOp",EDGE,"E7.0"),sQuery(id+"F8.wireOp",EDGE,"E10"),sQuery(id+"F8.wireOp",EDGE,"E11"),sQuery(id+"F8.wireOp",EDGE,"E12.1.0"),sQuery(id+"F8.wireOp",EDGE,"E12.1.1"),sQuery(id+"F8.wireOp",EDGE,"E12.2.0"),sQuery(id+"F8.wireOp",EDGE,"E12.2.1"),sQuery(id+"F8.wireOp",EDGE,"E12.3.0"),sQuery(id+"F8.wireOp",EDGE,"E12.3.1"),sQuery(id+"F8.wireOp",EDGE,"E12.4.0"),sQuery(id+"F8.wireOp",EDGE,"E12.4.1"),sQuery(id+"F8.wireOp",EDGE,"E12.5.0"),sQuery(id+"F8.wireOp",EDGE,"E12.5.1"),sQuery(id+"F8.wireOp",EDGE,"E12.6.0"),sQuery(id+"F8.wireOp",EDGE,"E13"),sQuery(id+"F8.wireOp",EDGE,"E14")])]}),"instanceName":"1"}),"instanceName":"2"});
            var Q3;
            Q3=makeQuery(id+"F18.opPattern","COPY",BODY,{"derivedFrom":makeQuery(id+"F13.opPattern","COPY",BODY,{"derivedFrom":makeQuery(id+"F9.opExtrude","SWEPT_BODY",BODY,{"disambiguationData":[OSD([sQuery(id+"F8.wireOp",EDGE,"E7.0"),sQuery(id+"F8.wireOp",EDGE,"E10"),sQuery(id+"F8.wireOp",EDGE,"E11"),sQuery(id+"F8.wireOp",EDGE,"E12.1.0"),sQuery(id+"F8.wireOp",EDGE,"E12.1.1"),sQuery(id+"F8.wireOp",EDGE,"E12.2.0"),sQuery(id+"F8.wireOp",EDGE,"E12.2.1"),sQuery(id+"F8.wireOp",EDGE,"E12.3.0"),sQuery(id+"F8.wireOp",EDGE,"E12.3.1"),sQuery(id+"F8.wireOp",EDGE,"E12.4.0"),sQuery(id+"F8.wireOp",EDGE,"E12.4.1"),sQuery(id+"F8.wireOp",EDGE,"E12.5.0"),sQuery(id+"F8.wireOp",EDGE,"E12.5.1"),sQuery(id+"F8.wireOp",EDGE,"E12.6.0"),sQuery(id+"F8.wireOp",EDGE,"E13"),sQuery(id+"F8.wireOp",EDGE,"E14")])]}),"instanceName":"2"}),"instanceName":"2"});
            var Q4;
            Q4=sQuery(id+"F31.wireOp",EDGE,"E35");
            circularPattern(context, id + "F32", {"entities" : qUnion([Q0, Q1, Q2, Q3]), "axis" : qUnion([Q4]), "angle" : 72 * degree, "instanceCount" : round(3), "oppositeDirection" : true});
        }
        {
            var Q0;
            Q0=makeQuery(id+"F6.opPattern","COPY",FACE,{"derivedFrom":makeQuery(id+"F3.opExtrude","CAP_FACE",FACE,{"disambiguationData":[OSD([sQuery(id+"F1.wireOp",EDGE,"E2.0"),sQuery(id+"F1.wireOp",EDGE,"E2.1"),sQuery(id+"F1.wireOp",EDGE,"E2.2"),sQuery(id+"F1.wireOp",EDGE,"E2.3"),sQuery(id+"F1.wireOp",EDGE,"E2.4"),sQuery(id+"F1.wireOp",EDGE,"E2.5")])],"isStart":true}),"instanceName":"2"});
            var sketch = newSketch(context, id + "F33", { "sketchPlane" : qUnion([Q0])});
            skLineSegment(sketch, "E36", {"start": v(-4.1, 7.1) * mm, "end": v(-17.1, 29.6) * mm});
            skSolve(sketch);
        }
        {
            var Q0;
            Q0=sQuery(id+"F33.wireOp",VERTEX,"E36.end");
            var Q1;
            Q1=sQuery(id+"F33.wireOp",VERTEX,"E36.start");
            var Q2;
            Q2=sQuery(id+"F11.wireOp",VERTEX,"E16.end");
            cPlane(context, id + "F34", {"entities" : qUnion([Q0, Q1, Q2]), "cplaneType" : CPlaneType.THREE_POINT, "offset" : 150 * mm, "width" : 150 * mm, "height" : 150 * mm});
        }
        {
            var Q0;
            Q0=qCreatedBy(id+"F34.planeOp",FACE);
            var sketch = newSketch(context, id + "F35", { "sketchPlane" : qUnion([Q0])});
            skLineSegment(sketch, "E37.0", {"start": v(10.32, 0) * mm, "end": v(30.97, -15.77) * mm});
            skLineSegment(sketch, "E38", {"start": v(20.65, -7.89) * mm, "end": v(38.57, 15.58) * mm});
            skSolve(sketch);
        }
        {
            var Q0;
            Q0=makeQuery(id+"F2.opExtrude","SWEPT_BODY",BODY,{"disambiguationData":[OSD([sQuery(id+"F0.wireOp",EDGE,"E0.0"),sQuery(id+"F0.wireOp",EDGE,"E0.1"),sQuery(id+"F0.wireOp",EDGE,"E0.2"),sQuery(id+"F0.wireOp",EDGE,"E0.3"),sQuery(id+"F0.wireOp",EDGE,"E0.4")])]});
            var Q1;
            Q1=sQuery(id+"F35.wireOp",EDGE,"E38");
            circularPattern(context, id + "F36", {"entities" : qUnion([Q0]), "axis" : qUnion([Q1]), "angle" : 120 * degree, "instanceCount" : round(3), "oppositeDirection" : true});
        }
        {
            var Q0;
            Q0=makeQuery(id+"F36.opPattern","COPY",FACE,{"derivedFrom":makeQuery(id+"F2.opExtrude","CAP_FACE",FACE,{"disambiguationData":[OSD([sQuery(id+"F0.wireOp",EDGE,"E0.0"),sQuery(id+"F0.wireOp",EDGE,"E0.1"),sQuery(id+"F0.wireOp",EDGE,"E0.2"),sQuery(id+"F0.wireOp",EDGE,"E0.3"),sQuery(id+"F0.wireOp",EDGE,"E0.4")])],"isStart":true}),"instanceName":"1"});
            var sketch = newSketch(context, id + "F37", { "sketchPlane" : qUnion([Q0])});
            skLineSegment(sketch, "E39", {"start": v(-4.5, -30.9) * mm, "end": v(1.45, -42.2) * mm});
            skPoint(sketch, "E40.orphan", {"position": v(-9.3, -21.76) * mm});
            skSolve(sketch);
        }
        {
            var Q0;
            Q0=sQuery(id+"F37.wireOp",VERTEX,"E39.end");
            var Q1;
            Q1=sQuery(id+"F37.wireOp",VERTEX,"E39.start");
            var Q2;
            Q2=sQuery(id+"F35.wireOp",VERTEX,"E38.end");
            cPlane(context, id + "F38", {"entities" : qUnion([Q0, Q1, Q2]), "cplaneType" : CPlaneType.THREE_POINT, "offset" : 150 * mm, "width" : 150 * mm, "height" : 150 * mm});
        }
        {
            var Q0;
            Q0=qCreatedBy(id+"F38.planeOp",FACE);
            var sketch = newSketch(context, id + "F39", { "sketchPlane" : qUnion([Q0])});
            skLineSegment(sketch, "E41.0", {"start": v(29.7, -11.34) * mm, "end": v(36.4, -22.2) * mm});
            skLineSegment(sketch, "E42", {"start": v(29.7, -11.34) * mm, "end": v(58.3, 6.33) * mm});
            skSolve(sketch);
        }
        {
            var Q0;
            Q0=makeQuery(id+"F22.opPattern","COPY",BODY,{"derivedFrom":makeQuery(id+"F17.opPattern","COPY",BODY,{"derivedFrom":makeQuery(id+"F3.opExtrude","SWEPT_BODY",BODY,{"disambiguationData":[OSD([sQuery(id+"F1.wireOp",EDGE,"E2.0"),sQuery(id+"F1.wireOp",EDGE,"E2.1"),sQuery(id+"F1.wireOp",EDGE,"E2.2"),sQuery(id+"F1.wireOp",EDGE,"E2.3"),sQuery(id+"F1.wireOp",EDGE,"E2.4"),sQuery(id+"F1.wireOp",EDGE,"E2.5")])]}),"instanceName":"1"}),"instanceName":"2"});
            var Q1;
            Q1=makeQuery(id+"F22.opPattern","COPY",BODY,{"derivedFrom":makeQuery(id+"F17.opPattern","COPY",BODY,{"derivedFrom":makeQuery(id+"F16.opPattern","COPY",BODY,{"derivedFrom":makeQuery(id+"F15.opPattern","COPY",BODY,{"derivedFrom":makeQuery(id+"F9.opExtrude","SWEPT_BODY",BODY,{"disambiguationData":[OSD([sQuery(id+"F8.wireOp",EDGE,"E7.0"),sQuery(id+"F8.wireOp",EDGE,"E10"),sQuery(id+"F8.wireOp",EDGE,"E11"),sQuery(id+"F8.wireOp",EDGE,"E12.1.0"),sQuery(id+"F8.wireOp",EDGE,"E12.1.1"),sQuery(id+"F8.wireOp",EDGE,"E12.2.0"),sQuery(id+"F8.wireOp",EDGE,"E12.2.1"),sQuery(id+"F8.wireOp",EDGE,"E12.3.0"),sQuery(id+"F8.wireOp",EDGE,"E12.3.1"),sQuery(id+"F8.wireOp",EDGE,"E12.4.0"),sQuery(id+"F8.wireOp",EDGE,"E12.4.1"),sQuery(id+"F8.wireOp",EDGE,"E12.5.0"),sQuery(id+"F8.wireOp",EDGE,"E12.5.1"),sQuery(id+"F8.wireOp",EDGE,"E12.6.0"),sQuery(id+"F8.wireOp",EDGE,"E13"),sQuery(id+"F8.wireOp",EDGE,"E14")])]}),"instanceName":"2"}),"instanceName":"1"}),"instanceName":"1"}),"instanceName":"2"});
            var Q2;
            Q2=makeQuery(id+"F22.opPattern","COPY",BODY,{"derivedFrom":makeQuery(id+"F17.opPattern","COPY",BODY,{"derivedFrom":makeQuery(id+"F13.opPattern","COPY",BODY,{"derivedFrom":makeQuery(id+"F9.opExtrude","SWEPT_BODY",BODY,{"disambiguationData":[OSD([sQuery(id+"F8.wireOp",EDGE,"E7.0"),sQuery(id+"F8.wireOp",EDGE,"E10"),sQuery(id+"F8.wireOp",EDGE,"E11"),sQuery(id+"F8.wireOp",EDGE,"E12.1.0"),sQuery(id+"F8.wireOp",EDGE,"E12.1.1"),sQuery(id+"F8.wireOp",EDGE,"E12.2.0"),sQuery(id+"F8.wireOp",EDGE,"E12.2.1"),sQuery(id+"F8.wireOp",EDGE,"E12.3.0"),sQuery(id+"F8.wireOp",EDGE,"E12.3.1"),sQuery(id+"F8.wireOp",EDGE,"E12.4.0"),sQuery(id+"F8.wireOp",EDGE,"E12.4.1"),sQuery(id+"F8.wireOp",EDGE,"E12.5.0"),sQuery(id+"F8.wireOp",EDGE,"E12.5.1"),sQuery(id+"F8.wireOp",EDGE,"E12.6.0"),sQuery(id+"F8.wireOp",EDGE,"E13"),sQuery(id+"F8.wireOp",EDGE,"E14")])]}),"instanceName":"1"}),"instanceName":"1"}),"instanceName":"2"});
            var Q3;
            Q3=makeQuery(id+"F18.opPattern","COPY",BODY,{"derivedFrom":makeQuery(id+"F13.opPattern","COPY",BODY,{"derivedFrom":makeQuery(id+"F9.opExtrude","SWEPT_BODY",BODY,{"disambiguationData":[OSD([sQuery(id+"F8.wireOp",EDGE,"E7.0"),sQuery(id+"F8.wireOp",EDGE,"E10"),sQuery(id+"F8.wireOp",EDGE,"E11"),sQuery(id+"F8.wireOp",EDGE,"E12.1.0"),sQuery(id+"F8.wireOp",EDGE,"E12.1.1"),sQuery(id+"F8.wireOp",EDGE,"E12.2.0"),sQuery(id+"F8.wireOp",EDGE,"E12.2.1"),sQuery(id+"F8.wireOp",EDGE,"E12.3.0"),sQuery(id+"F8.wireOp",EDGE,"E12.3.1"),sQuery(id+"F8.wireOp",EDGE,"E12.4.0"),sQuery(id+"F8.wireOp",EDGE,"E12.4.1"),sQuery(id+"F8.wireOp",EDGE,"E12.5.0"),sQuery(id+"F8.wireOp",EDGE,"E12.5.1"),sQuery(id+"F8.wireOp",EDGE,"E12.6.0"),sQuery(id+"F8.wireOp",EDGE,"E13"),sQuery(id+"F8.wireOp",EDGE,"E14")])]}),"instanceName":"2"}),"instanceName":"1"});
            var Q4;
            Q4=sQuery(id+"F39.wireOp",EDGE,"E42");
            circularPattern(context, id + "F40", {"entities" : qUnion([Q0, Q1, Q2, Q3]), "axis" : qUnion([Q4]), "angle" : 72 * degree, "instanceCount" : round(3), "oppositeDirection" : true});
        }
        {
            var Q0;
            Q0=makeQuery(id+"F36.opPattern","COPY",FACE,{"derivedFrom":makeQuery(id+"F2.opExtrude","CAP_FACE",FACE,{"disambiguationData":[OSD([sQuery(id+"F0.wireOp",EDGE,"E0.0"),sQuery(id+"F0.wireOp",EDGE,"E0.1"),sQuery(id+"F0.wireOp",EDGE,"E0.2"),sQuery(id+"F0.wireOp",EDGE,"E0.3"),sQuery(id+"F0.wireOp",EDGE,"E0.4")])],"isStart":true}),"instanceName":"2"});
            var sketch = newSketch(context, id + "F41", { "sketchPlane" : qUnion([Q0])});
            skLineSegment(sketch, "E43", {"start": v(0, -18.47) * mm, "end": v(0, -31.23) * mm});
            skPoint(sketch, "E44.orphan", {"position": v(0, -41.55) * mm});
            skSolve(sketch);
        }
        {
            var Q0;
            Q0=sQuery(id+"F41.wireOp",VERTEX,"E43.end");
            var Q1;
            Q1=sQuery(id+"F41.wireOp",VERTEX,"E43.start");
            var Q2;
            Q2=sQuery(id+"F11.wireOp",VERTEX,"E16.end");
            cPlane(context, id + "F42", {"entities" : qUnion([Q0, Q1, Q2]), "cplaneType" : CPlaneType.THREE_POINT, "offset" : 150 * mm, "width" : 150 * mm, "height" : 150 * mm});
        }
        {
            var Q0;
            Q0=qCreatedBy(id+"F42.planeOp",FACE);
            var sketch = newSketch(context, id + "F43", { "sketchPlane" : qUnion([Q0])});
            skLineSegment(sketch, "E45.0", {"start": v(-25.52, -7.89) * mm, "end": v(-31.23, -19.3) * mm});
            skLineSegment(sketch, "E46", {"start": v(-31.23, -19.3) * mm, "end": v(-78.41, 4.3) * mm});
            skSolve(sketch);
        }
        {
            var Q0;
            Q0=makeQuery(id+"F40.opPattern","COPY",BODY,{"derivedFrom":makeQuery(id+"F22.opPattern","COPY",BODY,{"derivedFrom":makeQuery(id+"F17.opPattern","COPY",BODY,{"derivedFrom":makeQuery(id+"F3.opExtrude","SWEPT_BODY",BODY,{"disambiguationData":[OSD([sQuery(id+"F1.wireOp",EDGE,"E2.0"),sQuery(id+"F1.wireOp",EDGE,"E2.1"),sQuery(id+"F1.wireOp",EDGE,"E2.2"),sQuery(id+"F1.wireOp",EDGE,"E2.3"),sQuery(id+"F1.wireOp",EDGE,"E2.4"),sQuery(id+"F1.wireOp",EDGE,"E2.5")])]}),"instanceName":"1"}),"instanceName":"2"}),"instanceName":"2"});
            var Q1;
            Q1=makeQuery(id+"F40.opPattern","COPY",BODY,{"derivedFrom":makeQuery(id+"F22.opPattern","COPY",BODY,{"derivedFrom":makeQuery(id+"F17.opPattern","COPY",BODY,{"derivedFrom":makeQuery(id+"F13.opPattern","COPY",BODY,{"derivedFrom":makeQuery(id+"F9.opExtrude","SWEPT_BODY",BODY,{"disambiguationData":[OSD([sQuery(id+"F8.wireOp",EDGE,"E7.0"),sQuery(id+"F8.wireOp",EDGE,"E10"),sQuery(id+"F8.wireOp",EDGE,"E11"),sQuery(id+"F8.wireOp",EDGE,"E12.1.0"),sQuery(id+"F8.wireOp",EDGE,"E12.1.1"),sQuery(id+"F8.wireOp",EDGE,"E12.2.0"),sQuery(id+"F8.wireOp",EDGE,"E12.2.1"),sQuery(id+"F8.wireOp",EDGE,"E12.3.0"),sQuery(id+"F8.wireOp",EDGE,"E12.3.1"),sQuery(id+"F8.wireOp",EDGE,"E12.4.0"),sQuery(id+"F8.wireOp",EDGE,"E12.4.1"),sQuery(id+"F8.wireOp",EDGE,"E12.5.0"),sQuery(id+"F8.wireOp",EDGE,"E12.5.1"),sQuery(id+"F8.wireOp",EDGE,"E12.6.0"),sQuery(id+"F8.wireOp",EDGE,"E13"),sQuery(id+"F8.wireOp",EDGE,"E14")])]}),"instanceName":"1"}),"instanceName":"1"}),"instanceName":"2"}),"instanceName":"2"});
            var Q2;
            Q2=makeQuery(id+"F40.opPattern","COPY",BODY,{"derivedFrom":makeQuery(id+"F18.opPattern","COPY",BODY,{"derivedFrom":makeQuery(id+"F13.opPattern","COPY",BODY,{"derivedFrom":makeQuery(id+"F9.opExtrude","SWEPT_BODY",BODY,{"disambiguationData":[OSD([sQuery(id+"F8.wireOp",EDGE,"E7.0"),sQuery(id+"F8.wireOp",EDGE,"E10"),sQuery(id+"F8.wireOp",EDGE,"E11"),sQuery(id+"F8.wireOp",EDGE,"E12.1.0"),sQuery(id+"F8.wireOp",EDGE,"E12.1.1"),sQuery(id+"F8.wireOp",EDGE,"E12.2.0"),sQuery(id+"F8.wireOp",EDGE,"E12.2.1"),sQuery(id+"F8.wireOp",EDGE,"E12.3.0"),sQuery(id+"F8.wireOp",EDGE,"E12.3.1"),sQuery(id+"F8.wireOp",EDGE,"E12.4.0"),sQuery(id+"F8.wireOp",EDGE,"E12.4.1"),sQuery(id+"F8.wireOp",EDGE,"E12.5.0"),sQuery(id+"F8.wireOp",EDGE,"E12.5.1"),sQuery(id+"F8.wireOp",EDGE,"E12.6.0"),sQuery(id+"F8.wireOp",EDGE,"E13"),sQuery(id+"F8.wireOp",EDGE,"E14")])]}),"instanceName":"2"}),"instanceName":"1"}),"instanceName":"2"});
            var Q3;
            Q3=makeQuery(id+"F40.opPattern","COPY",BODY,{"derivedFrom":makeQuery(id+"F22.opPattern","COPY",BODY,{"derivedFrom":makeQuery(id+"F17.opPattern","COPY",BODY,{"derivedFrom":makeQuery(id+"F16.opPattern","COPY",BODY,{"derivedFrom":makeQuery(id+"F15.opPattern","COPY",BODY,{"derivedFrom":makeQuery(id+"F9.opExtrude","SWEPT_BODY",BODY,{"disambiguationData":[OSD([sQuery(id+"F8.wireOp",EDGE,"E7.0"),sQuery(id+"F8.wireOp",EDGE,"E10"),sQuery(id+"F8.wireOp",EDGE,"E11"),sQuery(id+"F8.wireOp",EDGE,"E12.1.0"),sQuery(id+"F8.wireOp",EDGE,"E12.1.1"),sQuery(id+"F8.wireOp",EDGE,"E12.2.0"),sQuery(id+"F8.wireOp",EDGE,"E12.2.1"),sQuery(id+"F8.wireOp",EDGE,"E12.3.0"),sQuery(id+"F8.wireOp",EDGE,"E12.3.1"),sQuery(id+"F8.wireOp",EDGE,"E12.4.0"),sQuery(id+"F8.wireOp",EDGE,"E12.4.1"),sQuery(id+"F8.wireOp",EDGE,"E12.5.0"),sQuery(id+"F8.wireOp",EDGE,"E12.5.1"),sQuery(id+"F8.wireOp",EDGE,"E12.6.0"),sQuery(id+"F8.wireOp",EDGE,"E13"),sQuery(id+"F8.wireOp",EDGE,"E14")])]}),"instanceName":"2"}),"instanceName":"1"}),"instanceName":"1"}),"instanceName":"2"}),"instanceName":"2"});
            var Q4;
            Q4=sQuery(id+"F43.wireOp",EDGE,"E46");
            circularPattern(context, id + "F44", {"entities" : qUnion([Q0, Q1, Q2, Q3]), "axis" : qUnion([Q4]), "angle" : 72 * degree, "instanceCount" : round(3), "oppositeDirection" : true});
        }
        {
            var Q0;
            Q0=makeQuery(id+"F40.opPattern","COPY",FACE,{"derivedFrom":makeQuery(id+"F22.opPattern","COPY",FACE,{"derivedFrom":makeQuery(id+"F17.opPattern","COPY",FACE,{"derivedFrom":makeQuery(id+"F3.opExtrude","CAP_FACE",FACE,{"disambiguationData":[OSD([sQuery(id+"F1.wireOp",EDGE,"E2.0"),sQuery(id+"F1.wireOp",EDGE,"E2.1"),sQuery(id+"F1.wireOp",EDGE,"E2.2"),sQuery(id+"F1.wireOp",EDGE,"E2.3"),sQuery(id+"F1.wireOp",EDGE,"E2.4"),sQuery(id+"F1.wireOp",EDGE,"E2.5")])],"isStart":true}),"instanceName":"1"}),"instanceName":"2"}),"instanceName":"1"});
            var sketch = newSketch(context, id + "F45", { "sketchPlane" : qUnion([Q0])});
            skLineSegment(sketch, "E47", {"start": v(1.3, -21.26) * mm, "end": v(2.09, -34.23) * mm});
            skSolve(sketch);
        }
        {
            var Q0;
            Q0=sQuery(id+"F45.wireOp",VERTEX,"E47.end");
            var Q1;
            Q1=sQuery(id+"F45.wireOp",VERTEX,"E47.start");
            var Q2;
            Q2=makeQuery(id+"F6.opPattern","COPY",VERTEX,{"derivedFrom":makeQuery(id+"F3.opExtrude","CAP_VERTEX",VERTEX,{"disambiguationData":[OSD([sQuery(id+"F1.wireOp",EDGE,"E2.1"),sQuery(id+"F1.wireOp",EDGE,"E2.2")])],"isStart":true}),"instanceName":"3"});
            cPlane(context, id + "F46", {"entities" : qUnion([Q0, Q1, Q2]), "cplaneType" : CPlaneType.THREE_POINT, "offset" : 150 * mm, "width" : 150 * mm, "height" : 150 * mm});
        }
        {
            var Q0;
            Q0=qCreatedBy(id+"F46.planeOp",FACE);
            var sketch = newSketch(context, id + "F47", { "sketchPlane" : qUnion([Q0])});
            skLineSegment(sketch, "E48.0", {"start": v(-35.84, -28.53) * mm, "end": v(-33.4, -41.3) * mm});
            skLineSegment(sketch, "E49", {"start": v(-33.4, -41.3) * mm, "end": v(-61.9, -46.73) * mm});
            skSolve(sketch);
        }
        {
            var Q0;
            Q0=makeQuery(id+"F22.opPattern","COPY",BODY,{"derivedFrom":makeQuery(id+"F17.opPattern","COPY",BODY,{"derivedFrom":makeQuery(id+"F3.opExtrude","SWEPT_BODY",BODY,{"disambiguationData":[OSD([sQuery(id+"F1.wireOp",EDGE,"E2.0"),sQuery(id+"F1.wireOp",EDGE,"E2.1"),sQuery(id+"F1.wireOp",EDGE,"E2.2"),sQuery(id+"F1.wireOp",EDGE,"E2.3"),sQuery(id+"F1.wireOp",EDGE,"E2.4"),sQuery(id+"F1.wireOp",EDGE,"E2.5")])]}),"instanceName":"1"}),"instanceName":"2"});
            var Q1;
            Q1=makeQuery(id+"F22.opPattern","COPY",BODY,{"derivedFrom":makeQuery(id+"F17.opPattern","COPY",BODY,{"derivedFrom":makeQuery(id+"F13.opPattern","COPY",BODY,{"derivedFrom":makeQuery(id+"F9.opExtrude","SWEPT_BODY",BODY,{"disambiguationData":[OSD([sQuery(id+"F8.wireOp",EDGE,"E7.0"),sQuery(id+"F8.wireOp",EDGE,"E10"),sQuery(id+"F8.wireOp",EDGE,"E11"),sQuery(id+"F8.wireOp",EDGE,"E12.1.0"),sQuery(id+"F8.wireOp",EDGE,"E12.1.1"),sQuery(id+"F8.wireOp",EDGE,"E12.2.0"),sQuery(id+"F8.wireOp",EDGE,"E12.2.1"),sQuery(id+"F8.wireOp",EDGE,"E12.3.0"),sQuery(id+"F8.wireOp",EDGE,"E12.3.1"),sQuery(id+"F8.wireOp",EDGE,"E12.4.0"),sQuery(id+"F8.wireOp",EDGE,"E12.4.1"),sQuery(id+"F8.wireOp",EDGE,"E12.5.0"),sQuery(id+"F8.wireOp",EDGE,"E12.5.1"),sQuery(id+"F8.wireOp",EDGE,"E12.6.0"),sQuery(id+"F8.wireOp",EDGE,"E13"),sQuery(id+"F8.wireOp",EDGE,"E14")])]}),"instanceName":"1"}),"instanceName":"1"}),"instanceName":"2"});
            var Q2;
            Q2=makeQuery(id+"F22.opPattern","COPY",BODY,{"derivedFrom":makeQuery(id+"F17.opPattern","COPY",BODY,{"derivedFrom":makeQuery(id+"F16.opPattern","COPY",BODY,{"derivedFrom":makeQuery(id+"F15.opPattern","COPY",BODY,{"derivedFrom":makeQuery(id+"F9.opExtrude","SWEPT_BODY",BODY,{"disambiguationData":[OSD([sQuery(id+"F8.wireOp",EDGE,"E7.0"),sQuery(id+"F8.wireOp",EDGE,"E10"),sQuery(id+"F8.wireOp",EDGE,"E11"),sQuery(id+"F8.wireOp",EDGE,"E12.1.0"),sQuery(id+"F8.wireOp",EDGE,"E12.1.1"),sQuery(id+"F8.wireOp",EDGE,"E12.2.0"),sQuery(id+"F8.wireOp",EDGE,"E12.2.1"),sQuery(id+"F8.wireOp",EDGE,"E12.3.0"),sQuery(id+"F8.wireOp",EDGE,"E12.3.1"),sQuery(id+"F8.wireOp",EDGE,"E12.4.0"),sQuery(id+"F8.wireOp",EDGE,"E12.4.1"),sQuery(id+"F8.wireOp",EDGE,"E12.5.0"),sQuery(id+"F8.wireOp",EDGE,"E12.5.1"),sQuery(id+"F8.wireOp",EDGE,"E12.6.0"),sQuery(id+"F8.wireOp",EDGE,"E13"),sQuery(id+"F8.wireOp",EDGE,"E14")])]}),"instanceName":"2"}),"instanceName":"1"}),"instanceName":"1"}),"instanceName":"2"});
            var Q3;
            Q3=makeQuery(id+"F18.opPattern","COPY",BODY,{"derivedFrom":makeQuery(id+"F13.opPattern","COPY",BODY,{"derivedFrom":makeQuery(id+"F9.opExtrude","SWEPT_BODY",BODY,{"disambiguationData":[OSD([sQuery(id+"F8.wireOp",EDGE,"E7.0"),sQuery(id+"F8.wireOp",EDGE,"E10"),sQuery(id+"F8.wireOp",EDGE,"E11"),sQuery(id+"F8.wireOp",EDGE,"E12.1.0"),sQuery(id+"F8.wireOp",EDGE,"E12.1.1"),sQuery(id+"F8.wireOp",EDGE,"E12.2.0"),sQuery(id+"F8.wireOp",EDGE,"E12.2.1"),sQuery(id+"F8.wireOp",EDGE,"E12.3.0"),sQuery(id+"F8.wireOp",EDGE,"E12.3.1"),sQuery(id+"F8.wireOp",EDGE,"E12.4.0"),sQuery(id+"F8.wireOp",EDGE,"E12.4.1"),sQuery(id+"F8.wireOp",EDGE,"E12.5.0"),sQuery(id+"F8.wireOp",EDGE,"E12.5.1"),sQuery(id+"F8.wireOp",EDGE,"E12.6.0"),sQuery(id+"F8.wireOp",EDGE,"E13"),sQuery(id+"F8.wireOp",EDGE,"E14")])]}),"instanceName":"2"}),"instanceName":"1"});
            var Q4;
            Q4=sQuery(id+"F47.wireOp",EDGE,"E49");
            circularPattern(context, id + "F48", {"entities" : qUnion([Q0, Q1, Q2, Q3]), "axis" : qUnion([Q4]), "angle" : 120 * degree, "instanceCount" : 2, "oppositeDirection" : true});
        }
        {
            var Q0;
            Q0=makeQuery(id+"F26.opPattern","COPY",FACE,{"derivedFrom":makeQuery(id+"F3.opExtrude","CAP_FACE",FACE,{"disambiguationData":[OSD([sQuery(id+"F1.wireOp",EDGE,"E2.0"),sQuery(id+"F1.wireOp",EDGE,"E2.1"),sQuery(id+"F1.wireOp",EDGE,"E2.2"),sQuery(id+"F1.wireOp",EDGE,"E2.3"),sQuery(id+"F1.wireOp",EDGE,"E2.4"),sQuery(id+"F1.wireOp",EDGE,"E2.5")])],"isStart":true}),"instanceName":"1"});
            var sketch = newSketch(context, id + "F49", { "sketchPlane" : qUnion([Q0])});
            skLineSegment(sketch, "E50", {"start": v(-12.92, -27.06) * mm, "end": v(-2.09, -34.23) * mm});
            skSolve(sketch);
        }
        {
            var Q0;
            Q0=sQuery(id+"F49.wireOp",VERTEX,"E50.end");
            var Q1;
            Q1=sQuery(id+"F49.wireOp",VERTEX,"E50.start");
            var Q2;
            Q2=makeQuery(id+"F6.opPattern","COPY",VERTEX,{"derivedFrom":makeQuery(id+"F3.opExtrude","CAP_VERTEX",VERTEX,{"disambiguationData":[OSD([sQuery(id+"F1.wireOp",EDGE,"E2.0"),sQuery(id+"F1.wireOp",EDGE,"E2.5")])],"isStart":true}),"instanceName":"4"});
            cPlane(context, id + "F50", {"entities" : qUnion([Q0, Q1, Q2]), "cplaneType" : CPlaneType.THREE_POINT, "offset" : 150 * mm, "width" : 150 * mm, "height" : 150 * mm});
        }
        {
            var Q0;
            Q0=qCreatedBy(id+"F50.planeOp",FACE);
            var sketch = newSketch(context, id + "F51", { "sketchPlane" : qUnion([Q0])});
            skLineSegment(sketch, "E51.0", {"start": v(27.14, -5.92) * mm, "end": v(31.77, 6.22) * mm});
            skLineSegment(sketch, "E52", {"start": v(31.77, 6.22) * mm, "end": v(70.56, -8.6) * mm});
            skSolve(sketch);
        }
        {
            var Q0;
            Q0=makeQuery(id+"F16.opPattern","COPY",BODY,{"derivedFrom":makeQuery(id+"F15.opPattern","COPY",BODY,{"derivedFrom":makeQuery(id+"F9.opExtrude","SWEPT_BODY",BODY,{"disambiguationData":[OSD([sQuery(id+"F8.wireOp",EDGE,"E7.0"),sQuery(id+"F8.wireOp",EDGE,"E10"),sQuery(id+"F8.wireOp",EDGE,"E11"),sQuery(id+"F8.wireOp",EDGE,"E12.1.0"),sQuery(id+"F8.wireOp",EDGE,"E12.1.1"),sQuery(id+"F8.wireOp",EDGE,"E12.2.0"),sQuery(id+"F8.wireOp",EDGE,"E12.2.1"),sQuery(id+"F8.wireOp",EDGE,"E12.3.0"),sQuery(id+"F8.wireOp",EDGE,"E12.3.1"),sQuery(id+"F8.wireOp",EDGE,"E12.4.0"),sQuery(id+"F8.wireOp",EDGE,"E12.4.1"),sQuery(id+"F8.wireOp",EDGE,"E12.5.0"),sQuery(id+"F8.wireOp",EDGE,"E12.5.1"),sQuery(id+"F8.wireOp",EDGE,"E12.6.0"),sQuery(id+"F8.wireOp",EDGE,"E13"),sQuery(id+"F8.wireOp",EDGE,"E14")])]}),"instanceName":"1"}),"instanceName":"1"});
            var Q1;
            Q1=makeQuery(id+"F13.opPattern","COPY",BODY,{"derivedFrom":makeQuery(id+"F9.opExtrude","SWEPT_BODY",BODY,{"disambiguationData":[OSD([sQuery(id+"F8.wireOp",EDGE,"E7.0"),sQuery(id+"F8.wireOp",EDGE,"E10"),sQuery(id+"F8.wireOp",EDGE,"E11"),sQuery(id+"F8.wireOp",EDGE,"E12.1.0"),sQuery(id+"F8.wireOp",EDGE,"E12.1.1"),sQuery(id+"F8.wireOp",EDGE,"E12.2.0"),sQuery(id+"F8.wireOp",EDGE,"E12.2.1"),sQuery(id+"F8.wireOp",EDGE,"E12.3.0"),sQuery(id+"F8.wireOp",EDGE,"E12.3.1"),sQuery(id+"F8.wireOp",EDGE,"E12.4.0"),sQuery(id+"F8.wireOp",EDGE,"E12.4.1"),sQuery(id+"F8.wireOp",EDGE,"E12.5.0"),sQuery(id+"F8.wireOp",EDGE,"E12.5.1"),sQuery(id+"F8.wireOp",EDGE,"E12.6.0"),sQuery(id+"F8.wireOp",EDGE,"E13"),sQuery(id+"F8.wireOp",EDGE,"E14")])]}),"instanceName":"1"});
            var Q2;
            Q2=makeQuery(id+"F16.opPattern","COPY",BODY,{"derivedFrom":makeQuery(id+"F15.opPattern","COPY",BODY,{"derivedFrom":makeQuery(id+"F9.opExtrude","SWEPT_BODY",BODY,{"disambiguationData":[OSD([sQuery(id+"F8.wireOp",EDGE,"E7.0"),sQuery(id+"F8.wireOp",EDGE,"E10"),sQuery(id+"F8.wireOp",EDGE,"E11"),sQuery(id+"F8.wireOp",EDGE,"E12.1.0"),sQuery(id+"F8.wireOp",EDGE,"E12.1.1"),sQuery(id+"F8.wireOp",EDGE,"E12.2.0"),sQuery(id+"F8.wireOp",EDGE,"E12.2.1"),sQuery(id+"F8.wireOp",EDGE,"E12.3.0"),sQuery(id+"F8.wireOp",EDGE,"E12.3.1"),sQuery(id+"F8.wireOp",EDGE,"E12.4.0"),sQuery(id+"F8.wireOp",EDGE,"E12.4.1"),sQuery(id+"F8.wireOp",EDGE,"E12.5.0"),sQuery(id+"F8.wireOp",EDGE,"E12.5.1"),sQuery(id+"F8.wireOp",EDGE,"E12.6.0"),sQuery(id+"F8.wireOp",EDGE,"E13"),sQuery(id+"F8.wireOp",EDGE,"E14")])]}),"instanceName":"2"}),"instanceName":"1"});
            var Q3;
            Q3=makeQuery(id+"F3.opExtrude","SWEPT_BODY",BODY,{"disambiguationData":[OSD([sQuery(id+"F1.wireOp",EDGE,"E2.0"),sQuery(id+"F1.wireOp",EDGE,"E2.1"),sQuery(id+"F1.wireOp",EDGE,"E2.2"),sQuery(id+"F1.wireOp",EDGE,"E2.3"),sQuery(id+"F1.wireOp",EDGE,"E2.4"),sQuery(id+"F1.wireOp",EDGE,"E2.5")])]});
            var Q4;
            Q4=sQuery(id+"F51.wireOp",EDGE,"E52");
            circularPattern(context, id + "F52", {"entities" : qUnion([Q0, Q1, Q2, Q3]), "axis" : qUnion([Q4]), "angle" : 120 * degree, "instanceCount" : round(2), "oppositeDirection" : true});
        }
        {
            var Q0;
            Q0=makeQuery(id+"F32.opPattern","COPY",FACE,{"derivedFrom":makeQuery(id+"F26.opPattern","COPY",FACE,{"derivedFrom":makeQuery(id+"F3.opExtrude","CAP_FACE",FACE,{"disambiguationData":[OSD([sQuery(id+"F1.wireOp",EDGE,"E2.0"),sQuery(id+"F1.wireOp",EDGE,"E2.1"),sQuery(id+"F1.wireOp",EDGE,"E2.2"),sQuery(id+"F1.wireOp",EDGE,"E2.3"),sQuery(id+"F1.wireOp",EDGE,"E2.4"),sQuery(id+"F1.wireOp",EDGE,"E2.5")])],"isStart":true}),"instanceName":"2"}),"instanceName":"1"});
            var sketch = newSketch(context, id + "F53", { "sketchPlane" : qUnion([Q0])});
            skLineSegment(sketch, "E53", {"start": v(-10.6, -33.35) * mm, "end": v(-10.6, -18.35) * mm});
            skSolve(sketch);
        }
        {
            var Q0;
            Q0=sQuery(id+"F53.wireOp",VERTEX,"E53.start");
            var Q1;
            Q1=sQuery(id+"F53.wireOp",VERTEX,"E53.end");
            var Q2;
            Q2=makeQuery(id+"F32.opPattern","COPY",VERTEX,{"derivedFrom":makeQuery(id+"F26.opPattern","COPY",VERTEX,{"derivedFrom":makeQuery(id+"F3.opExtrude","CAP_VERTEX",VERTEX,{"disambiguationData":[OSD([sQuery(id+"F1.wireOp",EDGE,"E2.2"),sQuery(id+"F1.wireOp",EDGE,"E2.3")])],"isStart":false}),"instanceName":"2"}),"instanceName":"1"});
            cPlane(context, id + "F54", {"entities" : qUnion([Q0, Q1, Q2]), "cplaneType" : CPlaneType.THREE_POINT, "offset" : 150 * mm, "width" : 150 * mm, "height" : 150 * mm});
        }
        {
            var Q0;
            Q0=qCreatedBy(id+"F54.planeOp",FACE);
            var sketch = newSketch(context, id + "F55", { "sketchPlane" : qUnion([Q0])});
            skLineSegment(sketch, "E54.0", {"start": v(-2, -70.16) * mm, "end": v(-14.98, -62.66) * mm});
            skLineSegment(sketch, "E55", {"start": v(-14.98, -62.66) * mm, "end": v(-37.7, -102) * mm});
            skSolve(sketch);
        }
        {
            var Q0;
            Q0=makeQuery(id+"F26.opPattern","COPY",BODY,{"derivedFrom":makeQuery(id+"F3.opExtrude","SWEPT_BODY",BODY,{"disambiguationData":[OSD([sQuery(id+"F1.wireOp",EDGE,"E2.0"),sQuery(id+"F1.wireOp",EDGE,"E2.1"),sQuery(id+"F1.wireOp",EDGE,"E2.2"),sQuery(id+"F1.wireOp",EDGE,"E2.3"),sQuery(id+"F1.wireOp",EDGE,"E2.4"),sQuery(id+"F1.wireOp",EDGE,"E2.5")])]}),"instanceName":"2"});
            var Q1;
            Q1=makeQuery(id+"F26.opPattern","COPY",BODY,{"derivedFrom":makeQuery(id+"F16.opPattern","COPY",BODY,{"derivedFrom":makeQuery(id+"F15.opPattern","COPY",BODY,{"derivedFrom":makeQuery(id+"F9.opExtrude","SWEPT_BODY",BODY,{"disambiguationData":[OSD([sQuery(id+"F8.wireOp",EDGE,"E7.0"),sQuery(id+"F8.wireOp",EDGE,"E10"),sQuery(id+"F8.wireOp",EDGE,"E11"),sQuery(id+"F8.wireOp",EDGE,"E12.1.0"),sQuery(id+"F8.wireOp",EDGE,"E12.1.1"),sQuery(id+"F8.wireOp",EDGE,"E12.2.0"),sQuery(id+"F8.wireOp",EDGE,"E12.2.1"),sQuery(id+"F8.wireOp",EDGE,"E12.3.0"),sQuery(id+"F8.wireOp",EDGE,"E12.3.1"),sQuery(id+"F8.wireOp",EDGE,"E12.4.0"),sQuery(id+"F8.wireOp",EDGE,"E12.4.1"),sQuery(id+"F8.wireOp",EDGE,"E12.5.0"),sQuery(id+"F8.wireOp",EDGE,"E12.5.1"),sQuery(id+"F8.wireOp",EDGE,"E12.6.0"),sQuery(id+"F8.wireOp",EDGE,"E13"),sQuery(id+"F8.wireOp",EDGE,"E14")])]}),"instanceName":"2"}),"instanceName":"1"}),"instanceName":"2"});
            var Q2;
            Q2=makeQuery(id+"F26.opPattern","COPY",BODY,{"derivedFrom":makeQuery(id+"F13.opPattern","COPY",BODY,{"derivedFrom":makeQuery(id+"F9.opExtrude","SWEPT_BODY",BODY,{"disambiguationData":[OSD([sQuery(id+"F8.wireOp",EDGE,"E7.0"),sQuery(id+"F8.wireOp",EDGE,"E10"),sQuery(id+"F8.wireOp",EDGE,"E11"),sQuery(id+"F8.wireOp",EDGE,"E12.1.0"),sQuery(id+"F8.wireOp",EDGE,"E12.1.1"),sQuery(id+"F8.wireOp",EDGE,"E12.2.0"),sQuery(id+"F8.wireOp",EDGE,"E12.2.1"),sQuery(id+"F8.wireOp",EDGE,"E12.3.0"),sQuery(id+"F8.wireOp",EDGE,"E12.3.1"),sQuery(id+"F8.wireOp",EDGE,"E12.4.0"),sQuery(id+"F8.wireOp",EDGE,"E12.4.1"),sQuery(id+"F8.wireOp",EDGE,"E12.5.0"),sQuery(id+"F8.wireOp",EDGE,"E12.5.1"),sQuery(id+"F8.wireOp",EDGE,"E12.6.0"),sQuery(id+"F8.wireOp",EDGE,"E13"),sQuery(id+"F8.wireOp",EDGE,"E14")])]}),"instanceName":"1"}),"instanceName":"2"});
            var Q3;
            Q3=makeQuery(id+"F18.opPattern","COPY",BODY,{"derivedFrom":makeQuery(id+"F13.opPattern","COPY",BODY,{"derivedFrom":makeQuery(id+"F9.opExtrude","SWEPT_BODY",BODY,{"disambiguationData":[OSD([sQuery(id+"F8.wireOp",EDGE,"E7.0"),sQuery(id+"F8.wireOp",EDGE,"E10"),sQuery(id+"F8.wireOp",EDGE,"E11"),sQuery(id+"F8.wireOp",EDGE,"E12.1.0"),sQuery(id+"F8.wireOp",EDGE,"E12.1.1"),sQuery(id+"F8.wireOp",EDGE,"E12.2.0"),sQuery(id+"F8.wireOp",EDGE,"E12.2.1"),sQuery(id+"F8.wireOp",EDGE,"E12.3.0"),sQuery(id+"F8.wireOp",EDGE,"E12.3.1"),sQuery(id+"F8.wireOp",EDGE,"E12.4.0"),sQuery(id+"F8.wireOp",EDGE,"E12.4.1"),sQuery(id+"F8.wireOp",EDGE,"E12.5.0"),sQuery(id+"F8.wireOp",EDGE,"E12.5.1"),sQuery(id+"F8.wireOp",EDGE,"E12.6.0"),sQuery(id+"F8.wireOp",EDGE,"E13"),sQuery(id+"F8.wireOp",EDGE,"E14")])]}),"instanceName":"2"}),"instanceName":"2"});
            var Q4;
            Q4=sQuery(id+"F55.wireOp",EDGE,"E55");
            circularPattern(context, id + "F56", {"entities" : qUnion([Q0, Q1, Q2, Q3]), "axis" : qUnion([Q4]), "angle" : 120 * degree, "instanceCount" : 2, "oppositeDirection" : true});
        }
        {
            var Q0;
            Q0=makeQuery(id+"F56.opPattern","COPY",FACE,{"derivedFrom":makeQuery(id+"F26.opPattern","COPY",FACE,{"derivedFrom":makeQuery(id+"F3.opExtrude","CAP_FACE",FACE,{"disambiguationData":[OSD([sQuery(id+"F1.wireOp",EDGE,"E2.0"),sQuery(id+"F1.wireOp",EDGE,"E2.1"),sQuery(id+"F1.wireOp",EDGE,"E2.2"),sQuery(id+"F1.wireOp",EDGE,"E2.3"),sQuery(id+"F1.wireOp",EDGE,"E2.4"),sQuery(id+"F1.wireOp",EDGE,"E2.5")])],"isStart":true}),"instanceName":"2"}),"instanceName":"1"});
            var sketch = newSketch(context, id + "F57", { "sketchPlane" : qUnion([Q0])});
            skLineSegment(sketch, "E56", {"start": v(-34.48, 6) * mm, "end": v(-19.62, 8.02) * mm});
            skSolve(sketch);
        }
        {
            var Q0;
            Q0=sQuery(id+"F57.wireOp",VERTEX,"E56.start");
            var Q1;
            Q1=sQuery(id+"F57.wireOp",VERTEX,"E56.end");
            var Q2;
            Q2=makeQuery(id+"F56.opPattern","COPY",VERTEX,{"derivedFrom":makeQuery(id+"F26.opPattern","COPY",VERTEX,{"derivedFrom":makeQuery(id+"F3.opExtrude","CAP_VERTEX",VERTEX,{"disambiguationData":[OSD([sQuery(id+"F1.wireOp",EDGE,"E2.2"),sQuery(id+"F1.wireOp",EDGE,"E2.3")])],"isStart":false}),"instanceName":"2"}),"instanceName":"1"});
            cPlane(context, id + "F58", {"entities" : qUnion([Q0, Q1, Q2]), "cplaneType" : CPlaneType.THREE_POINT, "offset" : 150 * mm, "width" : 150 * mm, "height" : 150 * mm});
        }
        {
            var Q0;
            Q0=qCreatedBy(id+"F58.planeOp",FACE);
            var sketch = newSketch(context, id + "F59", { "sketchPlane" : qUnion([Q0])});
            skLineSegment(sketch, "E57.0", {"start": v(-8.72, -69.64) * mm, "end": v(-20.93, -60.93) * mm});
            skLineSegment(sketch, "E58", {"start": v(-20.93, -60.93) * mm, "end": v(-30.12, -73.8) * mm});
            skSolve(sketch);
        }
        {
            var Q0;
            Q0=makeQuery(id+"F52.opPattern","COPY",BODY,{"derivedFrom":makeQuery(id+"F3.opExtrude","SWEPT_BODY",BODY,{"disambiguationData":[OSD([sQuery(id+"F1.wireOp",EDGE,"E2.0"),sQuery(id+"F1.wireOp",EDGE,"E2.1"),sQuery(id+"F1.wireOp",EDGE,"E2.2"),sQuery(id+"F1.wireOp",EDGE,"E2.3"),sQuery(id+"F1.wireOp",EDGE,"E2.4"),sQuery(id+"F1.wireOp",EDGE,"E2.5")])]}),"instanceName":"1"});
            var Q1;
            Q1=makeQuery(id+"F52.opPattern","COPY",BODY,{"derivedFrom":makeQuery(id+"F16.opPattern","COPY",BODY,{"derivedFrom":makeQuery(id+"F15.opPattern","COPY",BODY,{"derivedFrom":makeQuery(id+"F9.opExtrude","SWEPT_BODY",BODY,{"disambiguationData":[OSD([sQuery(id+"F8.wireOp",EDGE,"E7.0"),sQuery(id+"F8.wireOp",EDGE,"E10"),sQuery(id+"F8.wireOp",EDGE,"E11"),sQuery(id+"F8.wireOp",EDGE,"E12.1.0"),sQuery(id+"F8.wireOp",EDGE,"E12.1.1"),sQuery(id+"F8.wireOp",EDGE,"E12.2.0"),sQuery(id+"F8.wireOp",EDGE,"E12.2.1"),sQuery(id+"F8.wireOp",EDGE,"E12.3.0"),sQuery(id+"F8.wireOp",EDGE,"E12.3.1"),sQuery(id+"F8.wireOp",EDGE,"E12.4.0"),sQuery(id+"F8.wireOp",EDGE,"E12.4.1"),sQuery(id+"F8.wireOp",EDGE,"E12.5.0"),sQuery(id+"F8.wireOp",EDGE,"E12.5.1"),sQuery(id+"F8.wireOp",EDGE,"E12.6.0"),sQuery(id+"F8.wireOp",EDGE,"E13"),sQuery(id+"F8.wireOp",EDGE,"E14")])]}),"instanceName":"2"}),"instanceName":"1"}),"instanceName":"1"});
            var Q2;
            Q2=makeQuery(id+"F52.opPattern","COPY",BODY,{"derivedFrom":makeQuery(id+"F16.opPattern","COPY",BODY,{"derivedFrom":makeQuery(id+"F15.opPattern","COPY",BODY,{"derivedFrom":makeQuery(id+"F9.opExtrude","SWEPT_BODY",BODY,{"disambiguationData":[OSD([sQuery(id+"F8.wireOp",EDGE,"E7.0"),sQuery(id+"F8.wireOp",EDGE,"E10"),sQuery(id+"F8.wireOp",EDGE,"E11"),sQuery(id+"F8.wireOp",EDGE,"E12.1.0"),sQuery(id+"F8.wireOp",EDGE,"E12.1.1"),sQuery(id+"F8.wireOp",EDGE,"E12.2.0"),sQuery(id+"F8.wireOp",EDGE,"E12.2.1"),sQuery(id+"F8.wireOp",EDGE,"E12.3.0"),sQuery(id+"F8.wireOp",EDGE,"E12.3.1"),sQuery(id+"F8.wireOp",EDGE,"E12.4.0"),sQuery(id+"F8.wireOp",EDGE,"E12.4.1"),sQuery(id+"F8.wireOp",EDGE,"E12.5.0"),sQuery(id+"F8.wireOp",EDGE,"E12.5.1"),sQuery(id+"F8.wireOp",EDGE,"E12.6.0"),sQuery(id+"F8.wireOp",EDGE,"E13"),sQuery(id+"F8.wireOp",EDGE,"E14")])]}),"instanceName":"1"}),"instanceName":"1"}),"instanceName":"1"});
            var Q3;
            Q3=makeQuery(id+"F52.opPattern","COPY",BODY,{"derivedFrom":makeQuery(id+"F13.opPattern","COPY",BODY,{"derivedFrom":makeQuery(id+"F9.opExtrude","SWEPT_BODY",BODY,{"disambiguationData":[OSD([sQuery(id+"F8.wireOp",EDGE,"E7.0"),sQuery(id+"F8.wireOp",EDGE,"E10"),sQuery(id+"F8.wireOp",EDGE,"E11"),sQuery(id+"F8.wireOp",EDGE,"E12.1.0"),sQuery(id+"F8.wireOp",EDGE,"E12.1.1"),sQuery(id+"F8.wireOp",EDGE,"E12.2.0"),sQuery(id+"F8.wireOp",EDGE,"E12.2.1"),sQuery(id+"F8.wireOp",EDGE,"E12.3.0"),sQuery(id+"F8.wireOp",EDGE,"E12.3.1"),sQuery(id+"F8.wireOp",EDGE,"E12.4.0"),sQuery(id+"F8.wireOp",EDGE,"E12.4.1"),sQuery(id+"F8.wireOp",EDGE,"E12.5.0"),sQuery(id+"F8.wireOp",EDGE,"E12.5.1"),sQuery(id+"F8.wireOp",EDGE,"E12.6.0"),sQuery(id+"F8.wireOp",EDGE,"E13"),sQuery(id+"F8.wireOp",EDGE,"E14")])]}),"instanceName":"1"}),"instanceName":"1"});
            var Q4;
            Q4=sQuery(id+"F59.wireOp",EDGE,"E58");
            circularPattern(context, id + "F60", {"entities" : qUnion([Q0, Q1, Q2, Q3]), "axis" : qUnion([Q4]), "angle" : 120 * degree, "instanceCount" : 2, "oppositeDirection" : true});
        }
        {
            var Q0;
            Q0=makeQuery(id+"F22.opPattern","COPY",BODY,{"derivedFrom":makeQuery(id+"F17.opPattern","COPY",BODY,{"derivedFrom":makeQuery(id+"F16.opPattern","COPY",BODY,{"derivedFrom":makeQuery(id+"F15.opPattern","COPY",BODY,{"derivedFrom":makeQuery(id+"F9.opExtrude","SWEPT_BODY",BODY,{"disambiguationData":[OSD([sQuery(id+"F8.wireOp",EDGE,"E7.0"),sQuery(id+"F8.wireOp",EDGE,"E10"),sQuery(id+"F8.wireOp",EDGE,"E11"),sQuery(id+"F8.wireOp",EDGE,"E12.1.0"),sQuery(id+"F8.wireOp",EDGE,"E12.1.1"),sQuery(id+"F8.wireOp",EDGE,"E12.2.0"),sQuery(id+"F8.wireOp",EDGE,"E12.2.1"),sQuery(id+"F8.wireOp",EDGE,"E12.3.0"),sQuery(id+"F8.wireOp",EDGE,"E12.3.1"),sQuery(id+"F8.wireOp",EDGE,"E12.4.0"),sQuery(id+"F8.wireOp",EDGE,"E12.4.1"),sQuery(id+"F8.wireOp",EDGE,"E12.5.0"),sQuery(id+"F8.wireOp",EDGE,"E12.5.1"),sQuery(id+"F8.wireOp",EDGE,"E12.6.0"),sQuery(id+"F8.wireOp",EDGE,"E13"),sQuery(id+"F8.wireOp",EDGE,"E14")])]}),"instanceName":"1"}),"instanceName":"1"}),"instanceName":"1"}),"instanceName":"1"});
            deleteBodies(context, id + "F61", {"entities" : qUnion([Q0])});
        }
        {
            var Q0;
            Q0=makeQuery(id+"F22.opPattern","COPY",BODY,{"derivedFrom":makeQuery(id+"F17.opPattern","COPY",BODY,{"derivedFrom":makeQuery(id+"F16.opPattern","COPY",BODY,{"derivedFrom":makeQuery(id+"F15.opPattern","COPY",BODY,{"derivedFrom":makeQuery(id+"F9.opExtrude","SWEPT_BODY",BODY,{"disambiguationData":[OSD([sQuery(id+"F8.wireOp",EDGE,"E7.0"),sQuery(id+"F8.wireOp",EDGE,"E10"),sQuery(id+"F8.wireOp",EDGE,"E11"),sQuery(id+"F8.wireOp",EDGE,"E12.1.0"),sQuery(id+"F8.wireOp",EDGE,"E12.1.1"),sQuery(id+"F8.wireOp",EDGE,"E12.2.0"),sQuery(id+"F8.wireOp",EDGE,"E12.2.1"),sQuery(id+"F8.wireOp",EDGE,"E12.3.0"),sQuery(id+"F8.wireOp",EDGE,"E12.3.1"),sQuery(id+"F8.wireOp",EDGE,"E12.4.0"),sQuery(id+"F8.wireOp",EDGE,"E12.4.1"),sQuery(id+"F8.wireOp",EDGE,"E12.5.0"),sQuery(id+"F8.wireOp",EDGE,"E12.5.1"),sQuery(id+"F8.wireOp",EDGE,"E12.6.0"),sQuery(id+"F8.wireOp",EDGE,"E13"),sQuery(id+"F8.wireOp",EDGE,"E14")])]}),"instanceName":"1"}),"instanceName":"1"}),"instanceName":"1"}),"instanceName":"2"});
            deleteBodies(context, id + "F62", {"entities" : qUnion([Q0])});
        }
        {
            var Q0;
            Q0=makeQuery(id+"F26.opPattern","COPY",BODY,{"derivedFrom":makeQuery(id+"F16.opPattern","COPY",BODY,{"derivedFrom":makeQuery(id+"F15.opPattern","COPY",BODY,{"derivedFrom":makeQuery(id+"F9.opExtrude","SWEPT_BODY",BODY,{"disambiguationData":[OSD([sQuery(id+"F8.wireOp",EDGE,"E7.0"),sQuery(id+"F8.wireOp",EDGE,"E10"),sQuery(id+"F8.wireOp",EDGE,"E11"),sQuery(id+"F8.wireOp",EDGE,"E12.1.0"),sQuery(id+"F8.wireOp",EDGE,"E12.1.1"),sQuery(id+"F8.wireOp",EDGE,"E12.2.0"),sQuery(id+"F8.wireOp",EDGE,"E12.2.1"),sQuery(id+"F8.wireOp",EDGE,"E12.3.0"),sQuery(id+"F8.wireOp",EDGE,"E12.3.1"),sQuery(id+"F8.wireOp",EDGE,"E12.4.0"),sQuery(id+"F8.wireOp",EDGE,"E12.4.1"),sQuery(id+"F8.wireOp",EDGE,"E12.5.0"),sQuery(id+"F8.wireOp",EDGE,"E12.5.1"),sQuery(id+"F8.wireOp",EDGE,"E12.6.0"),sQuery(id+"F8.wireOp",EDGE,"E13"),sQuery(id+"F8.wireOp",EDGE,"E14")])]}),"instanceName":"1"}),"instanceName":"1"}),"instanceName":"1"});
            deleteBodies(context, id + "F63", {"entities" : qUnion([Q0])});
        }
        {
            var Q0;
            Q0=makeQuery(id+"F26.opPattern","COPY",BODY,{"derivedFrom":makeQuery(id+"F16.opPattern","COPY",BODY,{"derivedFrom":makeQuery(id+"F15.opPattern","COPY",BODY,{"derivedFrom":makeQuery(id+"F9.opExtrude","SWEPT_BODY",BODY,{"disambiguationData":[OSD([sQuery(id+"F8.wireOp",EDGE,"E7.0"),sQuery(id+"F8.wireOp",EDGE,"E10"),sQuery(id+"F8.wireOp",EDGE,"E11"),sQuery(id+"F8.wireOp",EDGE,"E12.1.0"),sQuery(id+"F8.wireOp",EDGE,"E12.1.1"),sQuery(id+"F8.wireOp",EDGE,"E12.2.0"),sQuery(id+"F8.wireOp",EDGE,"E12.2.1"),sQuery(id+"F8.wireOp",EDGE,"E12.3.0"),sQuery(id+"F8.wireOp",EDGE,"E12.3.1"),sQuery(id+"F8.wireOp",EDGE,"E12.4.0"),sQuery(id+"F8.wireOp",EDGE,"E12.4.1"),sQuery(id+"F8.wireOp",EDGE,"E12.5.0"),sQuery(id+"F8.wireOp",EDGE,"E12.5.1"),sQuery(id+"F8.wireOp",EDGE,"E12.6.0"),sQuery(id+"F8.wireOp",EDGE,"E13"),sQuery(id+"F8.wireOp",EDGE,"E14")])]}),"instanceName":"1"}),"instanceName":"1"}),"instanceName":"2"});
            deleteBodies(context, id + "F64", {"entities" : qUnion([Q0])});
        }
    });
